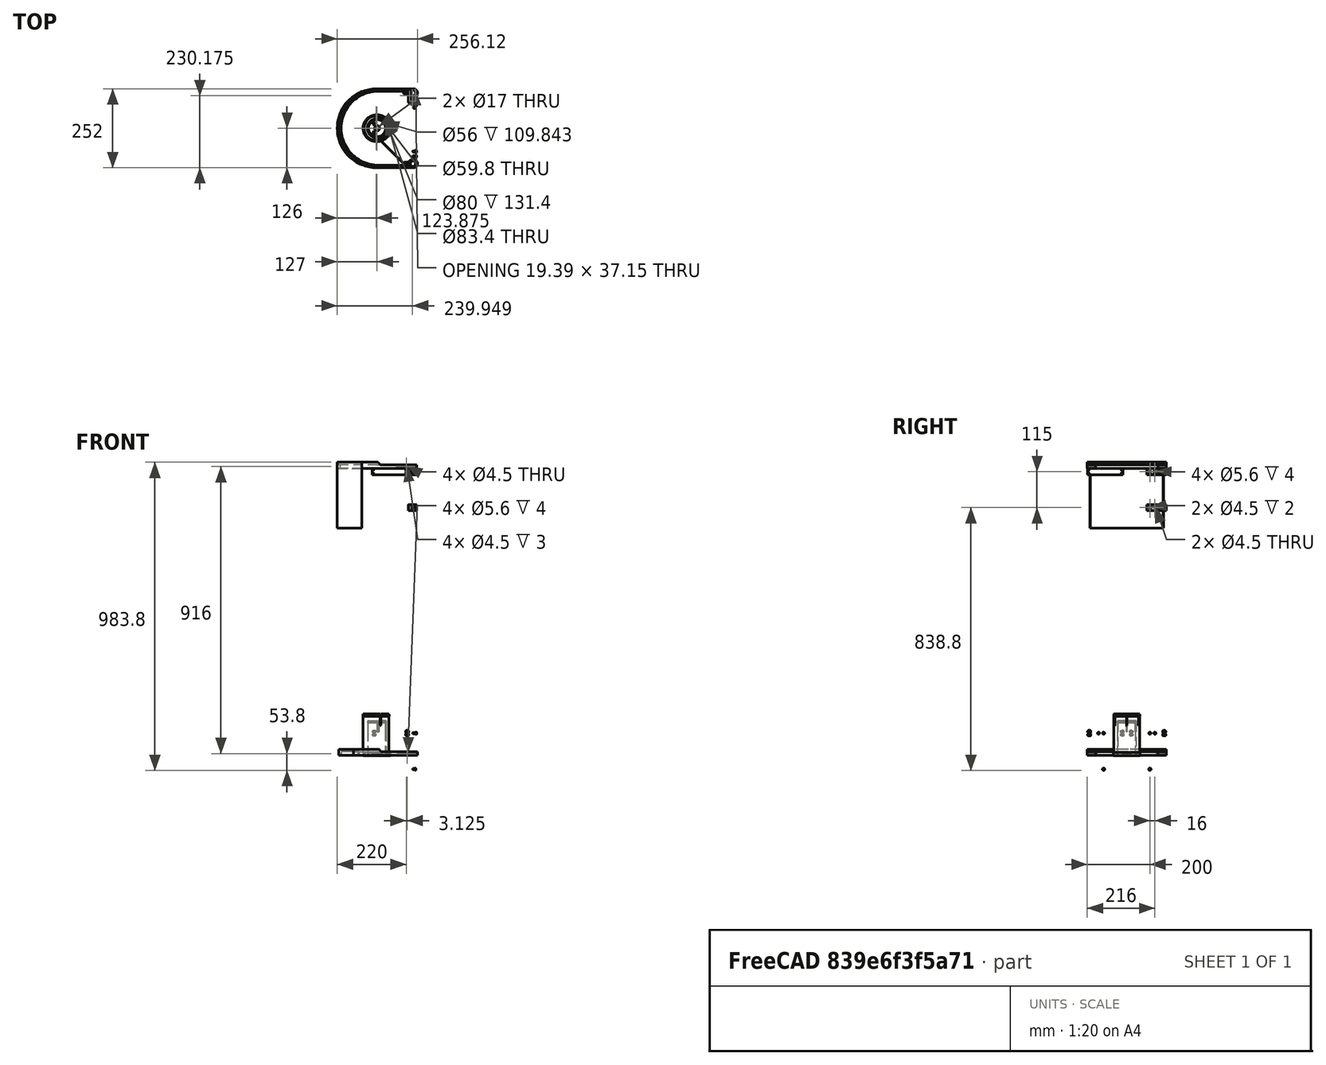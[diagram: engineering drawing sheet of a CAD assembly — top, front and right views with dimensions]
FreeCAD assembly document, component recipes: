
FREECAD ASSEMBLY — COMPONENT RECIPES ("Secondary")

This assembly document has 9 components, labeled P0..P8 below (a component is one placed body or linked part). 9 of them carry a construction recipe — the FreeCAD feature program that regenerates the part from scratch, quoted from this document or its linked companion documents; the rest are supplied as boundary geometry only. No exploded tour is included for this assembly.
COMPONENT P0 — recipe-attached ("SpiderVane", modeled in this document).
Construction recipe (the document's own serialized feature program — sketch geometry with constraints, then the solid features built on it; lengths are millimeters unless a unit is written):

FEATURE [PartDesign::ShapeBinder] ShapeBinder001  label="SpiderVane_ShapeBinder_Spider"
  Support = -> [Binder]
  TraceSupport = false
FEATURE [Sketcher::SketchObject] Sketch075  label="SpiderVane_Base_Sketch"
  ExternalGeometry = -> [ShapeBinder001]
  FullyConstrained = true
  MapMode = 5
  Support = -> [XY_Plane013]
  expr: Constraints[13] = <<Common>>#<<Parameters>>.sec_spiderwidth * 1.5
  expr: Constraints[5] = <<Common>>#<<Parameters>>.sec_spiderwidth
  expr: Constraints[6] = <<Common>>#<<Parameters>>.sec_sidebolt * 2.5
  sketch-geometry (5):
    g0: LineSegment StartX=-11.9668 StartY=-13.1925 StartZ=0 EndX=100.487 EndY=-125.646 EndZ=0
    g1: LineSegment StartX=100.487 StartY=-125.646 StartZ=0 EndX=101.194 EndY=-124.939 EndZ=0
    g2: LineSegment StartX=-11.9668 StartY=-13.1925 StartZ=0 EndX=-11.2596 EndY=-12.4854 EndZ=0
    g3: GeomPoint X=-4.18858 Y=-19.5565 Z=0
    g4: LineSegment StartX=-11.2596 StartY=-12.4854 StartZ=0 EndX=101.194 EndY=-124.939 EndZ=0
  constraints (15):
    c: Coincident(g2,g0)
    c: Perpendicular(g0,g2)
    c: Coincident(g0,g1)
    c: Coincident(g4,g2)
    c: Coincident(g4,g1)
    c: Distance(g1) = 1
    c: Distance(g2,g3) = 10
    c: Perpendicular(g4,g1)
    c: Parallel(g0,g4)
    c: PointOnObject(g3,g-3)
    c: PointOnObject(g3,g-5)
    c: PointOnObject(g2,g-3)
    c: PointOnObject(g1,g-3)
    c: Distance(g1,g-4) = 1.5
    c: Block(g1)
FEATURE [PartDesign::Pad] Pad011  label="SpiderVane_Base"
  Direction = (0,0,1)
  Length = 20
  Length2 = 100
  Profile = -> Sketch075
  Type = 0
  expr: Length = <<Common>>#<<Parameters>>.sec_stalkheight
FEATURE [Sketcher::SketchObject] Sketch076  label="SpiderVane_Hole_Sketch"
  ExternalGeometry = -> [Pad011]
  FullyConstrained = true
  MapMode = 5
  Placement = pos=(-12.5796,-12.5796,0) rot=(0.862856,-0.357407,-0.357407;1.71777rad)
  Support = -> [Pad011]
  expr: Constraints[0] = <<Common>>#<<Parameters>>.sec_collbolt * 1.1
  expr: Constraints[10] = <<Common>>#<<Parameters>>.sec_stalkheight / 2
  expr: Constraints[11] = <<Common>>#<<Parameters>>.sec_stalkheight / 2
  expr: Constraints[14] = <<Common>>#<<Parameters>>.sec_stalkheight / 4
  expr: Constraints[15] = <<Common>>#<<Parameters>>.sec_stalkheight / 4
  expr: Constraints[16] = <<Common>>#<<Parameters>>.sec_sidebolt * 1.25
  expr: Constraints[17] = <<Common>>#<<Parameters>>.sec_sidebolt * 1.25
  sketch-geometry (6):
    g0: Circle CenterX=5.86674 CenterY=15 CenterZ=0 NormalX=0 NormalY=0 NormalZ=1 AngleXU=0 Radius=2.2
    g1: Circle CenterX=5.86674 CenterY=5 CenterZ=0 NormalX=0 NormalY=0 NormalZ=1 AngleXU=0 Radius=2.2
    g2: Circle CenterX=154.901 CenterY=15 CenterZ=0 NormalX=0 NormalY=0 NormalZ=1 AngleXU=0 Radius=2.2
    g3: Circle CenterX=154.901 CenterY=5 CenterZ=0 NormalX=0 NormalY=0 NormalZ=1 AngleXU=0 Radius=2.2
    g4: LineSegment StartX=5.86674 StartY=15 StartZ=0 EndX=5.86674 EndY=0 EndZ=0
    g5: LineSegment StartX=154.901 StartY=15 StartZ=0 EndX=154.901 EndY=0 EndZ=0
  constraints (18):
    c: Diameter(g2) = 4.4
    c: Equal(g2,g3)
    c: Equal(g2,g0)
    c: Equal(g2,g1)
    c: Coincident(g4,g0)
    c: PointOnObject(g4,g-1)
    c: Vertical(g4)
    c: Coincident(g5,g2)
    c: PointOnObject(g5,g-1)
    c: Vertical(g5)
    c: DistanceY(g1,g0) = 10
    c: DistanceY(g3,g2) = 10
    c: PointOnObject(g1,g4)
    c: PointOnObject(g3,g5)
    c: DistanceY(g4,g1) = 5
    c: DistanceY(g5,g3) = 5
    c: DistanceX(g-3,g4) = 5
    c: DistanceX(g5,g-4) = 5
FEATURE [PartDesign::Hole] Hole032  label="SpiderVane_Hole"
  BaseFeature = -> Pad011
  CustomThreadClearance = 0
  Depth = 25
  DepthType = 1
  Diameter = 4.3
  DrillForDepth = false
  DrillPoint = 1
  DrillPointAngle = 118
  HoleCutCountersinkAngle = 90
  HoleCutCustomValues = false
  HoleCutDepth = 0
  HoleCutDiameter = 6.1
  HoleCutType = 0
  ModelThread = false
  Profile = -> Sketch076
  Tapered = false
  TaperedAngle = 90
  ThreadClass = 0
  ThreadDepth = 23.5
  ThreadDepthType = 0
  ThreadDirection = 0
  ThreadFit = 1
  ThreadSize = 11
  ThreadType = 1
  Threaded = false
  UseCustomThreadClearance = false
FEATURE [PartDesign::CoordinateSystem] Local_CS146  label="LCS_Vane_HubZF"
  AttacherType = Attacher::AttachEngine3D
  MapMode = 11
  Placement = pos=(-8.43122,-16.728,15) rot=(0.281085,0.678598,-0.678598;3.68962rad)
  Support = -> [Hole032]
FEATURE [PartDesign::CoordinateSystem] Local_CS147  label="LCS_Vane_HubZA"
  AttacherType = Attacher::AttachEngine3D
  MapMode = 11
  Placement = pos=(-7.72411,-16.0209,15) rot=(-0.862856,0.357407,-0.357407;1.71777rad)
  Support = -> [Hole032]
FEATURE [PartDesign::CoordinateSystem] Local_CS148  label="LCS_Vane_HubNF"
  AttacherType = Attacher::AttachEngine3D
  MapMode = 11
  Placement = pos=(-8.43122,-16.728,5) rot=(0.281085,0.678598,-0.678598;3.68962rad)
  Support = -> [Hole032]
FEATURE [PartDesign::CoordinateSystem] Local_CS149  label="LCS_Vane_HubNA"
  AttacherType = Attacher::AttachEngine3D
  MapMode = 11
  Placement = pos=(-7.72411,-16.0209,5) rot=(-0.862856,0.357407,-0.357407;1.71777rad)
  Support = -> [Hole032]
FEATURE [PartDesign::CoordinateSystem] Local_CS150  label="LCS_Vane_ClampZF"
  AttacherType = Attacher::AttachEngine3D
  MapMode = 11
  Placement = pos=(96.9516,-122.111,15) rot=(0.281085,0.678598,-0.678598;3.68962rad)
  Support = -> [Hole032]
FEATURE [PartDesign::CoordinateSystem] Local_CS151  label="LCS_Vane_ClampZA"
  AttacherType = Attacher::AttachEngine3D
  MapMode = 11
  Placement = pos=(97.6587,-121.404,15) rot=(-0.862856,0.357407,-0.357407;1.71777rad)
  Support = -> [Hole032]
FEATURE [PartDesign::CoordinateSystem] Local_CS152  label="LCS_Vane_ClampNF"
  AttacherType = Attacher::AttachEngine3D
  MapMode = 11
  Placement = pos=(96.9516,-122.111,5) rot=(0.281085,0.678598,-0.678598;3.68962rad)
  Support = -> [Hole032]
FEATURE [PartDesign::CoordinateSystem] Local_CS153  label="LCS_Vane_ClampNA"
  AttacherType = Attacher::AttachEngine3D
  MapMode = 11
  Placement = pos=(97.6587,-121.404,5) rot=(-0.862856,0.357407,-0.357407;1.71777rad)
  Support = -> [Hole032]
FEATURE [PartDesign::Body] Body011  label="SpiderVane"
  Group = -> [Sketch075,Pad011,Sketch076,Local_CS146,Local_CS147,Local_CS148,Local_CS149,Local_CS150,Local_CS151,Local_CS152,Local_CS153,Hole032,ShapeBinder001]
  Origin = -> Origin013
  Placement = pos=(-3.125,0,896) rot=(0,0,1;0rad)
  Tip = -> Hole032
  expr: .Placement.Base.x = -<<Common>>#<<Parameters>>.sec_offset_x
  expr: .Placement.Base.z = <<Common>>#<<Parameters>>.datum_sec_upperhub
COMPONENT P1 — recipe-attached ("UpperClamp", modeled in this document).
Construction recipe (the document's own serialized feature program — sketch geometry with constraints, then the solid features built on it; lengths are millimeters unless a unit is written):

FEATURE [PartDesign::ShapeBinder] ShapeBinder002  label="UpperClamp_ShapeBinder_Spider"
  Support = -> [Binder]
  TraceSupport = false
FEATURE [Sketcher::SketchObject] Sketch086  label="UpperClamp_Structure_Sketch"
  ExternalGeometry = -> [ShapeBinder002]
  FullyConstrained = true
  MapMode = 5
  Support = -> [XY_Plane060]
  expr: Constraints[18] = <<Common>>#<<Parameters>>.sec_fthick - <<Common>>#<<Parameters>>.pri_tol
  expr: Constraints[19] = <<Common>>#<<Parameters>>.sec_spthick
  expr: Constraints[31] = <<Common>>#<<Parameters>>.sec_fthick + 4 - <<Common>>#<<Parameters>>.sec_sidebolt * 1.25
  expr: Constraints[38] = <<Common>>#<<Parameters>>.sec_fillet
  expr: Constraints[39] = <<Common>>#<<Parameters>>.sec_sidebolt * 5.5
  expr: Constraints[40] = <<Common>>#<<Parameters>>.sec_fillet
  expr: Constraints[47] = <<Common>>#<<Parameters>>.sec_fthick / 2
  expr: Constraints[58] = <<Common>>#<<Parameters>>.sec_fillet / 2
  expr: Constraints[59] = <<Common>>#<<Parameters>>.sec_fthick * 1.5
  expr: Constraints[60] = <<Common>>#<<Parameters>>.sec_fthick * 2
  expr: Constraints[68] = <<Common>>#<<Parameters>>.sec_sidebolt_y
  expr: Constraints[6] = <<Common>>#<<Parameters>>.sec_sidebolt * 2.5 + <<Common>>#<<Parameters>>.sec_spiderwidth * 1.5
  expr: Constraints[70] = <<Common>>#<<Parameters>>.sec_fthick * 2
  expr: Constraints[88] = <<Common>>#<<Parameters>>.sec_sidebolt * 3.5 - <<Common>>#<<Parameters>>.sec_fillet
  expr: Constraints[93] = <<Common>>#<<Parameters>>.sec_sidebolt_y - <<Common>>#<<Parameters>>.sec_sidebolt * 6
  sketch-geometry (34):
    g0: LineSegment StartX=124.125 StartY=100.5 StartZ=0 EndX=124.125 EndY=64 EndZ=0
    g1: LineSegment StartX=118.125 StartY=103.094 StartZ=0 EndX=118.125 EndY=86 EndZ=0
    g2: ArcOfCircle CenterX=116.125 CenterY=113 CenterZ=0 NormalX=0 NormalY=0 NormalZ=1 AngleXU=0 Radius=13 StartAngle=0 EndAngle=1.5708
    g3: LineSegment StartX=116.125 StartY=126 StartZ=0 EndX=102.255 EndY=126 EndZ=0
    g4: LineSegment StartX=94.1232 StartY=117.868 StartZ=0 EndX=106.508 EndY=104.253 EndZ=0
    g5: LineSegment StartX=102.255 StartY=126 StartZ=0 EndX=94.1232 EndY=117.868 EndZ=0
    g6: LineSegment StartX=120.125 StartY=64 StartZ=0 EndX=124.125 EndY=64 EndZ=0
    g7: LineSegment StartX=116.125 StartY=126 StartZ=0 EndX=116.125 EndY=113 EndZ=0
    g8: LineSegment StartX=116.125 StartY=113 StartZ=0 EndX=129.125 EndY=113 EndZ=0
    g9: LineSegment StartX=124.125 StartY=100.5 StartZ=0 EndX=125.125 EndY=100.5 EndZ=0
    g10: LineSegment StartX=129.125 StartY=113 StartZ=0 EndX=129.125 EndY=109.881 EndZ=0
    g11: ArcOfCircle CenterX=116.125 CenterY=109.881 CenterZ=0 NormalX=0 NormalY=0 NormalZ=1 AngleXU=0 Radius=13 StartAngle=5.47707 EndAngle=6.28319
    g12: LineSegment StartX=116.125 StartY=109.881 StartZ=0 EndX=129.125 EndY=109.881 EndZ=0
    g13: LineSegment StartX=102.255 StartY=126 StartZ=0 EndX=92.709 EndY=116.454 EndZ=0
    g14: LineSegment StartX=92.709 StartY=116.454 StartZ=0 EndX=111.539 EndY=97.6238 EndZ=0
    g15: LineSegment StartX=112.125 StartY=96.2096 StartZ=0 EndX=112.125 EndY=83.6569 EndZ=0
    g16: LineSegment StartX=116.625 StartY=102.662 StartZ=0 EndX=116.625 EndY=86 EndZ=0
    g17: ArcOfCircle CenterX=120.125 CenterY=66 CenterZ=0 NormalX=0 NormalY=0 NormalZ=1 AngleXU=0 Radius=2 StartAngle=3.14159 EndAngle=4.71239
    g18: ArcOfCircle CenterX=110.125 CenterY=96.2096 CenterZ=0 NormalX=0 NormalY=0 NormalZ=1 AngleXU=0 Radius=2 StartAngle=1.6e-15 EndAngle=0.785398
    g19: ArcOfCircle CenterX=116.125 CenterY=113 CenterZ=0 NormalX=0 NormalY=0 NormalZ=1 AngleXU=0 Radius=9.35 StartAngle=5.00646 EndAngle=10.9472
    g20: LineSegment StartX=118.125 StartY=86 StartZ=0 EndX=116.625 EndY=86 EndZ=0
    g21: LineSegment StartX=118.125 StartY=66 StartZ=0 EndX=120.125 EndY=66 EndZ=0
    g22: LineSegment StartX=120.125 StartY=66 StartZ=0 EndX=120.125 EndY=64 EndZ=0
    g23: ArcOfCircle CenterX=115.625 CenterY=102.662 CenterZ=0 NormalX=0 NormalY=0 NormalZ=1 AngleXU=0 Radius=1 StartAngle=1.2e-15 EndAngle=1.52247
    g24: ArcOfCircle CenterX=119.125 CenterY=103.094 CenterZ=0 NormalX=0 NormalY=0 NormalZ=1 AngleXU=0 Radius=1 StartAngle=1.86487 EndAngle=3.14159
    g25: LineSegment StartX=112.125 StartY=90 StartZ=0 EndX=116.625 EndY=90 EndZ=0
    g26: ArcOfCircle CenterX=114.125 CenterY=83.6569 CenterZ=0 NormalX=0 NormalY=0 NormalZ=1 AngleXU=0 Radius=2 StartAngle=3.14159 EndAngle=3.92699
    g27: ArcOfCircle CenterX=116.125 CenterY=76 CenterZ=0 NormalX=0 NormalY=0 NormalZ=1 AngleXU=0 Radius=2 StartAngle=-1.8e-15 EndAngle=0.785398
    g28: LineSegment StartX=112.711 StartY=82.2426 StartZ=0 EndX=117.539 EndY=77.4142 EndZ=0
    g29: LineSegment StartX=118.125 StartY=76 StartZ=0 EndX=118.125 EndY=66 EndZ=0
    g30: LineSegment StartX=112.125 StartY=83.6569 StartZ=0 EndX=114.125 EndY=83.6569 EndZ=0
    g31: LineSegment StartX=114.125 StartY=83.6569 StartZ=0 EndX=112.711 EndY=82.2426 EndZ=0
    g32: LineSegment StartX=117.539 StartY=77.4142 StartZ=0 EndX=116.125 EndY=76 EndZ=0
    g33: LineSegment StartX=116.125 StartY=76 StartZ=0 EndX=118.125 EndY=76 EndZ=0
  constraints (96):
    c: Vertical(g0)
    c: Vertical(g1)
    c: Coincident(g3,g2)
    c: Horizontal(g3)
    c: Coincident(g5,g3)
    c: Coincident(g5,g4)
    c: Distance(g5) = 11.5
    c: Horizontal(g6)
    c: Vertical(g7)
    c: Coincident(g7,g2)
    c: PointOnObject(g4,g-6)
    c: Parallel(g5,g-6)
    c: Coincident(g2,g-4)
    c: PointOnObject(g0,g-5)
    c: Coincident(g8,g2)
    c: Horizontal(g8)
    c: Coincident(g9,g0)
    c: Horizontal(g9)
    c: DistanceY(g0,g-5) = 2.5
    c: DistanceX(g9,g9) = 1
    c: Coincident(g10,g2)
    c: Vertical(g10)
    c: Coincident(g11,g10)
    c: Coincident(g11,g9)
    c: Coincident(g12,g11)
    c: Coincident(g12,g10)
    c: Horizontal(g12)
    c: Equal(g11,g2)
    c: PointOnObject(g2,g-4)
    c: Coincident(g13,g3)
    c: PointOnObject(g13,g-6)
    c: Distance(g13,g4) = 2
    c: Coincident(g14,g13)
    c: Tangent(g4,g-4)
    c: PointOnObject(g4,g-4)
    c: Perpendicular(g-6,g14)
    c: Vertical(g15)
    c: Vertical(g16)
    c: Radius(g17) = 2
    c: DistanceY(g6,g16) = 22
    c: Radius(g18) = 2
    c: Tangent(g18,g15) = 1.5708
    c: Tangent(g18,g14) = 1.5708
    c: Coincident(g19,g2)
    c: Coincident(g20,g1)
    c: Coincident(g20,g16)
    c: Horizontal(g20)
    c: DistanceX(g20,g20) = 1.5
    c: Coincident(g17,g6)
    c: Coincident(g21,g17)
    c: Horizontal(g21)
    c: Coincident(g22,g17)
    c: Coincident(g22,g6)
    c: Vertical(g22)
    c: Coincident(g7,g2)
    c: Coincident(g7,g8)
    c: Tangent(g19,g23) = 1.5708
    c: Tangent(g16,g23) = 1.5708
    c: Radius(g23) = 1
    c: DistanceX(g15,g16) = 4.5
    c: DistanceX(g1,g0) = 6
    c: Tangent(g19,g24) = 1.5708
    c: Tangent(g1,g24) = -1.5708
    c: Equal(g24,g23)
    c: PointOnObject(g19,g-3)
    c: PointOnObject(g25,g15)
    c: Horizontal(g25)
    c: PointOnObject(g25,g16)
    c: DistanceY(g25) = 90
    c: Coincident(g17,g21)
    c: DistanceX(g17,g0) = 6
    c: Coincident(g26,g15)
    c: Coincident(g28,g26)
    c: Coincident(g28,g27)
    c: Coincident(g29,g27)
    c: Coincident(g29,g17)
    c: Vertical(g29)
    c: Coincident(g30,g15)
    c: Coincident(g30,g26)
    c: Coincident(g31,g26)
    c: Coincident(g31,g26)
    c: Coincident(g32,g27)
    c: Coincident(g32,g27)
    c: Coincident(g33,g27)
    c: Coincident(g33,g27)
    c: Horizontal(g33)
    c: Horizontal(g30)
    c: Equal(g26,g27)
    c: DistanceY(g6,g27) = 12
    c: Perpendicular(g28,g32)
    c: Perpendicular(g28,g31)
    c: Angle(g30,g31) = 0.785398
    c: DistanceX(g15,g17) = 6  'ClampHeight'
    c: DistanceY(g17) = 66
    c: Coincident(g6,g0)
    c: Equal(g27,g17)
FEATURE [PartDesign::Plane] DatumPlane025  label="UpperClamp_DatumPlane_Side"
  AttachmentOffset = pos=(0,0,0) rot=(0,0,1;1.5708rad)
  Length = 67.3781
  MapMode = 14
  Placement = pos=(124.125,0,0) rot=(0.707107,0,0.707107;3.14159rad)
  ResizeMode = 0
  Support = -> [ShapeBinder002,X_Axis060]
  Width = 168.378
FEATURE [Sketcher::SketchObject] Sketch085  label="UpperClamp_SideHole_Sketch"
  FullyConstrained = true
  MapMode = 5
  Placement = pos=(124.125,0,0) rot=(0.707107,0,0.707107;3.14159rad)
  Support = -> [DatumPlane025]
  expr: Constraints[0] = <<Common>>#<<Parameters>>.sec_sidebolt * 1.1
  expr: Constraints[5] = <<Common>>#<<Parameters>>.sec_stalkheight / 2
  expr: Constraints[6] = <<Common>>#<<Parameters>>.sec_sidebolt * 4
  expr: Constraints[7] = <<Common>>#<<Parameters>>.sec_sidebolt_y
  sketch-geometry (3):
    g0: Circle CenterX=10 CenterY=-74 CenterZ=0 NormalX=0 NormalY=0 NormalZ=1 AngleXU=0 Radius=2.2
    g1: Circle CenterX=10 CenterY=-90 CenterZ=0 NormalX=0 NormalY=0 NormalZ=1 AngleXU=0 Radius=2.2
    g2: LineSegment StartX=10 StartY=-74 StartZ=0 EndX=10 EndY=-90 EndZ=0
  constraints (8):
    c: Diameter(g0) = 4.4
    c: Equal(g0,g1)
    c: Coincident(g2,g0)
    c: Coincident(g2,g1)
    c: Vertical(g2)
    c: DistanceX(g2) = 10
    c: DistanceY(g2,g2) = 16
    c: DistanceY(g1,g-1) = 90
FEATURE [PartDesign::Pad] Pad031  label="UpperClamp_Structure"
  Direction = (0,0,1)
  Length = 20
  Length2 = 100
  Profile = -> Sketch086
  Type = 0
  expr: Length = <<Common>>#<<Parameters>>.sec_stalkheight
FEATURE [PartDesign::Plane] DatumPlane026  label="UpperClamp_DatumPlane_Spider"
  Length = 236.529
  MapMode = 14
  Placement = pos=(-11.8725,11.8725,0) rot=(-0.281085,0.678598,0.678598;3.68962rad)
  ResizeMode = 0
  Support = -> [ShapeBinder002,Z_Axis060]
  Width = 70.7729
FEATURE [Sketcher::SketchObject] Sketch087  label="UpperClamp_SpiderHole_Sketch"
  ExternalGeometry = -> [ShapeBinder002]
  FullyConstrained = true
  MapMode = 5
  Placement = pos=(-11.8725,11.8725,0) rot=(-0.281085,0.678598,0.678598;3.68962rad)
  Support = -> [DatumPlane026]
  expr: Constraints[0] = <<Common>>#<<Parameters>>.sec_collbolt * 1.1
  expr: Constraints[2] = <<Common>>#<<Parameters>>.sec_stalkheight / 2
  expr: Constraints[7] = <<Common>>#<<Parameters>>.sec_stalkheight / 4
  expr: Constraints[8] = <<Common>>#<<Parameters>>.sec_sidebolt * 1.25 + <<Common>>#<<Parameters>>.sec_spiderwidth * 1.5
  sketch-geometry (3):
    g0: Circle CenterX=-154.901 CenterY=5 CenterZ=0 NormalX=0 NormalY=0 NormalZ=1 AngleXU=0 Radius=2.2
    g1: Circle CenterX=-154.901 CenterY=15 CenterZ=0 NormalX=0 NormalY=0 NormalZ=1 AngleXU=0 Radius=2.2
    g2: LineSegment StartX=-154.901 StartY=15 StartZ=0 EndX=-154.901 EndY=0 EndZ=0
  constraints (9):
    c: Diameter(g0) = 4.4
    c: Equal(g0,g1)
    c: DistanceY(g0,g1) = 10
    c: Coincident(g2,g1)
    c: PointOnObject(g2,g-1)
    c: PointOnObject(g0,g2)
    c: Vertical(g2)
    c: DistanceY(g2,g0) = 5
    c: DistanceX(g-3,g2) = 6.5
FEATURE [PartDesign::Plane] DatumPlane032  label="UpperClamp_DatumPlane_SpiderNut"
  AttachmentOffset = pos=(0,0,-3) rot=(0,0,1;0rad)
  Length = 236.529
  MapMode = 5
  Placement = pos=(-9.75121,9.75121,0) rot=(-0.281085,0.678598,0.678598;3.68962rad)
  ResizeMode = 0
  Support = -> [DatumPlane026]
  Width = 70.7729
  expr: .AttachmentOffset.Base.z = -<<Common>>#<<Parameters>>.sec_fthick
FEATURE [PartDesign::CoordinateSystem] Local_CS275  label="LCS_UpperClamp_PoleTop"
  AttacherType = Attacher::AttachEngine3D
  AttachmentOffset = pos=(0,0,20) rot=(0,0,1;0rad)
  MapMode = 11
  Placement = pos=(116.125,113,20) rot=(0,0,1;1.5708rad)
  Support = -> [ShapeBinder002]
  expr: .AttachmentOffset.Base.z = <<Common>>#<<Parameters>>.sec_stalkheight
FEATURE [PartDesign::CoordinateSystem] Local_CS290  label="LCS_UpperClamp_PoleBottom"
  AttacherType = Attacher::AttachEngine3D
  MapMode = 11
  Placement = pos=(116.125,113,0) rot=(0.707107,-0.707107,0;3.14159rad)
  Support = -> [ShapeBinder002]
FEATURE [Sketcher::SketchObject] Sketch284  label="UpperClamp_SpiderNut_Sketch"
  AttachmentOffset = pos=(0,0,-3) rot=(0,0,1;0rad)
  ExternalGeometry = -> [Sketch087]
  FullyConstrained = true
  MapMode = 5
  Placement = pos=(-9.75121,9.75121,0) rot=(-0.281085,0.678598,0.678598;3.68962rad)
  Support = -> [DatumPlane026]
  expr: Constraints[14] = 7 + Common#<<Parameters>>.acc_FDMtol
  expr: Constraints[28] = <<Common>>#<<Parameters>>.sec_stalkheight / 4 + 1
  sketch-geometry (21):
    g0: LineSegment StartX=-158.551 StartY=21 StartZ=0 EndX=-158.551 EndY=11.35 EndZ=0
    g1: LineSegment StartX=-158.551 StartY=11.35 StartZ=0 EndX=-151.251 EndY=11.35 EndZ=0
    g2: LineSegment StartX=-151.251 StartY=11.35 StartZ=0 EndX=-151.251 EndY=21 EndZ=0
    g3: LineSegment StartX=-151.251 StartY=21 StartZ=0 EndX=-158.551 EndY=21 EndZ=0
    g4: LineSegment StartX=-158.551 StartY=-1 StartZ=0 EndX=-158.551 EndY=8.65 EndZ=0
    g5: LineSegment StartX=-158.551 StartY=8.65 StartZ=0 EndX=-151.251 EndY=8.65 EndZ=0
    g6: LineSegment StartX=-151.251 StartY=8.65 StartZ=0 EndX=-151.251 EndY=-1 EndZ=0
    g7: LineSegment StartX=-151.251 StartY=-1 StartZ=0 EndX=-158.551 EndY=-1 EndZ=0
    g8: LineSegment StartX=-154.901 StartY=15 StartZ=0 EndX=-154.901 EndY=5 EndZ=0
    g9: LineSegment StartX=-158.551 StartY=8.65 StartZ=0 EndX=-154.901 EndY=5 EndZ=0
    g10: LineSegment StartX=-154.901 StartY=15 StartZ=0 EndX=-151.251 EndY=11.35 EndZ=0
    g11: LineSegment StartX=-158.551 StartY=21 StartZ=0 EndX=-158.551 EndY=12.8927 EndZ=0
    g12: LineSegment StartX=-151.251 StartY=21 StartZ=0 EndX=-151.251 EndY=12.8927 EndZ=0
    g13: LineSegment StartX=-151.251 StartY=-1 StartZ=0 EndX=-151.251 EndY=7.10733 EndZ=0
    g14: LineSegment StartX=-158.551 StartY=-1 StartZ=0 EndX=-158.551 EndY=7.10733 EndZ=0
    g15: LineSegment StartX=-158.551 StartY=7.10733 StartZ=0 EndX=-154.901 EndY=9.21466 EndZ=0
    g16: LineSegment StartX=-151.251 StartY=7.10733 StartZ=0 EndX=-154.901 EndY=9.21466 EndZ=0
    g17: LineSegment StartX=-158.551 StartY=12.8927 StartZ=0 EndX=-154.901 EndY=10.7853 EndZ=0
    g18: LineSegment StartX=-151.251 StartY=12.8927 StartZ=0 EndX=-154.901 EndY=10.7853 EndZ=0
    g19: LineSegment StartX=-154.901 StartY=15 StartZ=0 EndX=-151.251 EndY=12.8927 EndZ=0
    g20: LineSegment StartX=-151.251 StartY=7.10733 StartZ=0 EndX=-154.901 EndY=5 EndZ=0
  constraints (55):
    c: Vertical(g0)
    c: Coincident(g2,g1)
    c: Vertical(g2)
    c: Coincident(g3,g2)
    c: Coincident(g3,g0)
    c: Vertical(g4)
    c: Coincident(g6,g5)
    c: Vertical(g6)
    c: Coincident(g7,g6)
    c: Coincident(g7,g4)
    c: Horizontal(g3)
    c: Equal(g3,g7)
    c: Horizontal(g7)
    c: Equal(g4,g0)
    c: DistanceX(g3,g3) = 7.3
    c: Coincident(g5,g4)
    c: Coincident(g1,g0)
    c: Horizontal(g5)
    c: Symmetric(g0,g1,g8)
    c: PointOnObject(g4,g0)
    c: Coincident(g8,g-4)
    c: Coincident(g8,g-3)
    c: Coincident(g9,g4)
    c: Coincident(g9,g8)
    c: Coincident(g10,g8)
    c: Coincident(g10,g1)
    c: Equal(g9,g10)
    c: Angle(g8,g10) = 0.785398
    c: DistanceY(g8,g2) = 6
    c: Coincident(g11,g3)
    c: Vertical(g11)
    c: Coincident(g12,g3)
    c: Vertical(g12)
    c: Coincident(g13,g7)
    c: Vertical(g13)
    c: Coincident(g14,g7)
    c: Vertical(g14)
    c: Coincident(g15,g14)
    c: PointOnObject(g15,g8)
    c: Coincident(g16,g13)
    c: Coincident(g16,g15)
    c: Coincident(g17,g11)
    c: PointOnObject(g17,g8)
    c: Coincident(g18,g12)
    c: Coincident(g18,g17)
    c: Equal(g18,g17)
    c: Equal(g17,g15)
    c: Equal(g15,g16)
    c: Angle(g18,g17) = 2.0944
    c: Coincident(g19,g8)
    c: Coincident(g19,g12)
    c: Coincident(g20,g13)
    c: Coincident(g20,g8)
    c: Equal(g20,g16)
    c: Equal(g18,g19)
FEATURE [Sketcher::SketchObject] Sketch  label="UpperClamp_ClampBump_Sketch"
  AttachmentOffset = pos=(0,0,10) rot=(0,0,1;0rad)
  ExternalGeometry = -> [ShapeBinder002]
  FullyConstrained = true
  MapMode = 5
  Placement = pos=(0,0,10) rot=(0,0,1;0rad)
  Support = -> [XY_Plane060]
  expr: .AttachmentOffset.Base.z = <<Common>>#<<Parameters>>.sec_stalkheight / 2
  expr: Constraints[70] = <<Common>>#<<Parameters>>.sec_poledia
  sketch-geometry (26):
    g0: LineSegment StartX=107.487 StartY=116.578 StartZ=0 EndX=124.763 EndY=109.422 EndZ=0
    g1: LineSegment StartX=112.547 StartY=121.638 StartZ=0 EndX=119.703 EndY=104.362 EndZ=0
    g2: LineSegment StartX=119.703 StartY=121.638 StartZ=0 EndX=112.547 EndY=104.362 EndZ=0
    g3: LineSegment StartX=124.763 StartY=116.578 StartZ=0 EndX=107.487 EndY=109.422 EndZ=0
    g4: LineSegment StartX=107.487 StartY=116.578 StartZ=0 EndX=112.547 EndY=121.638 EndZ=0
    g5: LineSegment StartX=112.547 StartY=121.638 StartZ=0 EndX=119.703 EndY=121.638 EndZ=0
    g6: LineSegment StartX=119.703 StartY=121.638 StartZ=0 EndX=124.763 EndY=116.578 EndZ=0
    g7: LineSegment StartX=124.763 StartY=116.578 StartZ=0 EndX=124.763 EndY=109.422 EndZ=0
    g8: ArcOfCircle CenterX=119.703 CenterY=104.362 CenterZ=0 NormalX=0 NormalY=0 NormalZ=1 AngleXU=0 Radius=0.35 StartAngle=0.411417 EndAngle=3.51557
    g9: ArcOfCircle CenterX=124.763 CenterY=109.422 CenterZ=0 NormalX=0 NormalY=0 NormalZ=1 AngleXU=0 Radius=0.35 StartAngle=1.19681 EndAngle=4.30097
    g10: ArcOfCircle CenterX=124.763 CenterY=116.578 CenterZ=0 NormalX=0 NormalY=0 NormalZ=1 AngleXU=0 Radius=0.35 StartAngle=1.98221 EndAngle=5.08637
    g11: ArcOfCircle CenterX=119.703 CenterY=121.638 CenterZ=0 NormalX=0 NormalY=0 NormalZ=1 AngleXU=0 Radius=0.35 StartAngle=2.76761 EndAngle=5.87177
    g12: ArcOfCircle CenterX=112.547 CenterY=121.638 CenterZ=0 NormalX=0 NormalY=0 NormalZ=1 AngleXU=0 Radius=0.35 StartAngle=3.55301 EndAngle=6.65717
    g13: ArcOfCircle CenterX=107.487 CenterY=116.578 CenterZ=0 NormalX=0 NormalY=0 NormalZ=1 AngleXU=0 Radius=0.35 StartAngle=4.33841 EndAngle=7.44256
    g14: ArcOfCircle CenterX=107.487 CenterY=109.422 CenterZ=0 NormalX=0 NormalY=0 NormalZ=1 AngleXU=0 Radius=0.35 StartAngle=5.12381 EndAngle=8.22796
    g15: ArcOfCircle CenterX=112.547 CenterY=104.362 CenterZ=0 NormalX=0 NormalY=0 NormalZ=1 AngleXU=0 Radius=0.35 StartAngle=5.9092 EndAngle=9.01336
    g16: ArcOfCircle CenterX=116.125 CenterY=113 CenterZ=0 NormalX=0 NormalY=0 NormalZ=1 AngleXU=0 Radius=9.35 StartAngle=5.06765 EndAngle=5.14252
    g17: ArcOfCircle CenterX=116.125 CenterY=113 CenterZ=0 NormalX=0 NormalY=0 NormalZ=1 AngleXU=0 Radius=9.35 StartAngle=5.85305 EndAngle=5.92792
    g18: ArcOfCircle CenterX=116.125 CenterY=113 CenterZ=0 NormalX=0 NormalY=0 NormalZ=1 AngleXU=0 Radius=9.35 StartAngle=0.355264 EndAngle=0.430134
    g19: ArcOfCircle CenterX=116.125 CenterY=113 CenterZ=0 NormalX=0 NormalY=0 NormalZ=1 AngleXU=0 Radius=9.35 StartAngle=1.14066 EndAngle=1.21553
    g20: ArcOfCircle CenterX=116.125 CenterY=113 CenterZ=0 NormalX=0 NormalY=0 NormalZ=1 AngleXU=0 Radius=9.35 StartAngle=1.92606 EndAngle=2.00093
    g21: ArcOfCircle CenterX=116.125 CenterY=113 CenterZ=0 NormalX=0 NormalY=0 NormalZ=1 AngleXU=0 Radius=9.35 StartAngle=2.71146 EndAngle=2.78633
    g22: ArcOfCircle CenterX=116.125 CenterY=113 CenterZ=0 NormalX=0 NormalY=0 NormalZ=1 AngleXU=0 Radius=9.35 StartAngle=3.49686 EndAngle=3.57173
    g23: ArcOfCircle CenterX=116.125 CenterY=113 CenterZ=0 NormalX=0 NormalY=0 NormalZ=1 AngleXU=0 Radius=9.35 StartAngle=4.28225 EndAngle=4.35713
    g24: GeomPoint X=119.569 Y=104.685 Z=0
    g25: GeomPoint X=112.681 Y=121.315 Z=0
  constraints (76):
    c: PointOnObject(g0,g-3)
    c: PointOnObject(g0,g-3)
    c: PointOnObject(g1,g-3)
    c: PointOnObject(g1,g-3)
    c: PointOnObject(g2,g-3)
    c: PointOnObject(g2,g-3)
    c: PointOnObject(g3,g-3)
    c: PointOnObject(g3,g-3)
    c: Coincident(g4,g0)
    c: Coincident(g5,g1)
    c: Coincident(g6,g2)
    c: Coincident(g7,g3)
    c: Coincident(g4,g1)
    c: Coincident(g5,g2)
    c: Coincident(g6,g3)
    c: Equal(g4,g5)
    c: Equal(g5,g6)
    c: Coincident(g7,g0)
    c: Equal(g7,g5)
    c: Horizontal(g5)
    c: Coincident(g8,g1)
    c: PointOnObject(g8,g-3)
    c: Coincident(g9,g0)
    c: PointOnObject(g9,g-3)
    c: Coincident(g10,g3)
    c: PointOnObject(g10,g-3)
    c: Coincident(g11,g2)
    c: PointOnObject(g11,g-3)
    c: Coincident(g12,g1)
    c: PointOnObject(g12,g-3)
    c: Coincident(g13,g0)
    c: PointOnObject(g13,g-3)
    c: Coincident(g14,g3)
    c: PointOnObject(g14,g-3)
    c: Coincident(g15,g2)
    c: PointOnObject(g15,g-3)
    c: Coincident(g16,g8)
    c: Coincident(g16,g8)
    c: Coincident(g17,g16)
    c: Coincident(g17,g9)
    c: Coincident(g17,g9)
    c: Coincident(g18,g16)
    c: Coincident(g18,g10)
    c: Coincident(g18,g10)
    c: Coincident(g19,g16)
    c: Coincident(g19,g11)
    c: Coincident(g19,g11)
    c: Coincident(g20,g16)
    c: Coincident(g20,g12)
    c: Coincident(g20,g12)
    c: Coincident(g21,g16)
    c: Coincident(g21,g13)
    c: Coincident(g21,g13)
    c: Coincident(g22,g16)
    c: Coincident(g22,g14)
    c: Coincident(g22,g14)
    c: Coincident(g23,g16)
    c: Coincident(g23,g15)
    c: Coincident(g23,g15)
    c: Equal(g8,g9)
    c: Equal(g9,g10)
    c: Equal(g10,g11)
    c: Equal(g11,g12)
    c: Equal(g12,g13)
    c: Equal(g13,g14)
    c: Equal(g14,g15)
    c: PointOnObject(g24,g8)
    c: PointOnObject(g24,g1)
    c: PointOnObject(g25,g12)
    c: PointOnObject(g25,g1)
    c: Distance(g25,g24) = 18
    c: PointOnObject(g16,g0)
    c: PointOnObject(g16,g1)
    c: PointOnObject(g16,g2)
    c: PointOnObject(g16,g3)
    c: Coincident(g16,g-3)
FEATURE [PartDesign::Pad] Pad  label="UpperClamp_ClampBump"
  BaseFeature = -> Pad031
  Direction = (0,0,1)
  Length = 18.4
  Length2 = 10
  Midplane = true
  Profile = -> Sketch
  ReferenceAxis = -> Sketch [N_Axis]
  Type = 0
  expr: Length = <<Common>>#<<Parameters>>.sec_stalkheight - 1.6
FEATURE [Sketcher::SketchObject] Sketch285  label="UpperClamp_BumpGrad_Sketch"
  AttachmentOffset = pos=(0,0,0) rot=(1,0,0;1.5708rad)
  ExternalGeometry = -> [ShapeBinder002]
  FullyConstrained = true
  MapMode = 11
  Placement = pos=(116.125,113,0) rot=(0.57735,0.57735,0.57735;2.0944rad)
  Support = -> [ShapeBinder002]
  expr: Constraints[21] = <<Common>>#<<Parameters>>.sec_stalkheight
  expr: Constraints[25] = <<Common>>#<<Parameters>>.sec_poledia / 2
  expr: Constraints[26] = <<Common>>#<<Parameters>>.sec_clamptol * 5
  sketch-geometry (10):
    g0: LineSegment StartX=0 StartY=0 StartZ=0 EndX=0 EndY=20 EndZ=0
    g1: LineSegment StartX=0 StartY=20 StartZ=0 EndX=9.75 EndY=20 EndZ=0
    g2: LineSegment StartX=0 StartY=0 StartZ=0 EndX=9.75 EndY=0 EndZ=0
    g3: LineSegment StartX=9.75 StartY=20 StartZ=0 EndX=9.35 EndY=19.6 EndZ=0
    g4: LineSegment StartX=9.35 StartY=19.6 StartZ=0 EndX=9.35 EndY=19.2 EndZ=0
    g5: LineSegment StartX=9.35 StartY=19.2 StartZ=0 EndX=9 EndY=15.7 EndZ=0
    g6: LineSegment StartX=9 StartY=15.7 StartZ=0 EndX=9 EndY=4.3 EndZ=0
    g7: LineSegment StartX=9 StartY=4.3 StartZ=0 EndX=9.35 EndY=0.8 EndZ=0
    g8: LineSegment StartX=9.35 StartY=0.8 StartZ=0 EndX=9.35 EndY=0.4 EndZ=0
    g9: LineSegment StartX=9.35 StartY=0.4 StartZ=0 EndX=9.75 EndY=0 EndZ=0
  constraints (29):
    c: Coincident(g0,g-1)
    c: Vertical(g0)
    c: Coincident(g1,g0)
    c: Horizontal(g1)
    c: Coincident(g2,g0)
    c: Horizontal(g2)
    c: Coincident(g3,g1)
    c: Coincident(g4,g3)
    c: Vertical(g4)
    c: Coincident(g5,g4)
    c: Coincident(g6,g5)
    c: Vertical(g6)
    c: Coincident(g7,g6)
    c: Coincident(g8,g7)
    c: Vertical(g8)
    c: Coincident(g9,g8)
    c: Coincident(g9,g2)
    c: Equal(g9,g3)
    c: Equal(g8,g4)
    c: Equal(g5,g7)
    c: Equal(g2,g1)
    c: DistanceY(g0,g0) = 20
    c: DistanceY(g4,g4) = 0.4
    c: PointOnObject(g-3,g4)
    c: PointOnObject(g-3,g8)
    c: DistanceX(g5) = 9
    c: DistanceY(g5,g4) = 3.5
    c: Angle(g1,g3) = 0.785398
    c: DistanceY(g3,g1) = 0.4
FEATURE [PartDesign::Line] DatumLine  label="UpperClamp_DatumLine_Pole"
  AttacherType = Attacher::AttachEngineLine
  Length = 20
  MapMode = 19
  Placement = pos=(116.125,113,0) rot=(0,0,1;0rad)
  ResizeMode = 0
  Support = -> [ShapeBinder002]
FEATURE [PartDesign::Groove] Groove  label="UpperClamp_BumpGrad"
  Angle = 360
  Axis = (0,0,1)
  Base = (116.125,113,0)
  BaseFeature = -> Pad
  Profile = -> Sketch285
  ReferenceAxis = -> DatumLine
FEATURE [PartDesign::Hole] Hole  label="UpperClamp_SideHole"
  BaseFeature = -> Groove
  CustomThreadClearance = 0
  Depth = 150.759
  DepthType = 1
  Diameter = 4.5
  DrillForDepth = false
  DrillPoint = 1
  DrillPointAngle = 118
  HoleCutCountersinkAngle = 90
  HoleCutCustomValues = false
  HoleCutDepth = 4
  HoleCutDiameter = 5.6
  HoleCutType = 1
  ModelThread = false
  Profile = -> Sketch085
  Tapered = false
  TaperedAngle = 90
  ThreadClass = 0
  ThreadDepth = 150.759
  ThreadDepthType = 0
  ThreadDirection = 0
  ThreadFit = 0
  ThreadSize = 11
  ThreadType = 1
  Threaded = false
  UseCustomThreadClearance = false
  expr: HoleCutDiameter = <<Common>>#<<Parameters>>.acc_M4Bore
FEATURE [PartDesign::CoordinateSystem] Local_CS176  label="LCS_UpperClampNut_I"
  AttacherType = Attacher::AttachEngine3D
  MapMode = 11
  Placement = pos=(124.125,90,10) rot=(0.57735,-0.57735,-0.57735;2.0944rad)
  Support = -> [Hole]
FEATURE [PartDesign::CoordinateSystem] Local_CS177  label="LCS_UpperClampNut_O"
  AttacherType = Attacher::AttachEngine3D
  MapMode = 11
  Placement = pos=(124.125,74,10) rot=(0.57735,-0.57735,-0.57735;2.0944rad)
  Support = -> [Hole]
FEATURE [PartDesign::CoordinateSystem] Local_CS178  label="LCS_UpperClampBolt_I"
  AttacherType = Attacher::AttachEngine3D
  AttachmentOffset = pos=(0,0,1) rot=(0,0,1;0rad)
  MapMode = 11
  Placement = pos=(125.125,90,10) rot=(0.57735,0.57735,0.57735;2.0944rad)
  Support = -> [Hole]
  expr: .AttachmentOffset.Base.z = <<Common>>#<<Parameters>>.sec_spthick
FEATURE [PartDesign::CoordinateSystem] Local_CS179  label="LCS_UpperClampBolt_O"
  AttacherType = Attacher::AttachEngine3D
  AttachmentOffset = pos=(0,0,1) rot=(0,0,1;0rad)
  MapMode = 11
  Placement = pos=(125.125,74,10) rot=(0.57735,0.57735,0.57735;2.0944rad)
  Support = -> [Hole]
  expr: .AttachmentOffset.Base.z = <<Common>>#<<Parameters>>.sec_spthick
FEATURE [PartDesign::CoordinateSystem] Local_CS181  label="LCS_UpperClampPlate"
  AttacherType = Attacher::AttachEngine3D
  MapMode = 11
  Placement = pos=(124.125,90,10) rot=(0.57735,0.57735,0.57735;2.0944rad)
  Support = -> [Hole]
FEATURE [PartDesign::Hole] Hole052  label="UpperClamp_SpiderHole"
  BaseFeature = -> Hole
  CustomThreadClearance = 0
  Depth = 8
  DepthType = 0
  Diameter = 4.5
  DrillForDepth = false
  DrillPoint = 1
  DrillPointAngle = 118
  HoleCutCountersinkAngle = 90
  HoleCutCustomValues = false
  HoleCutDepth = 0
  HoleCutDiameter = 6.1
  HoleCutType = 0
  ModelThread = false
  Profile = -> Sketch087
  Tapered = false
  TaperedAngle = 90
  ThreadClass = 0
  ThreadDepth = 8
  ThreadDepthType = 0
  ThreadDirection = 0
  ThreadFit = 0
  ThreadSize = 11
  ThreadType = 1
  Threaded = false
  UseCustomThreadClearance = false
FEATURE [PartDesign::CoordinateSystem] Local_CS175  label="LCS_ClampSpider_Z"
  AttacherType = Attacher::AttachEngine3D
  MapMode = 11
  Placement = pos=(97.6587,121.404,15) rot=(-0.862856,-0.357407,0.357407;1.71777rad)
  Support = -> [Hole052]
FEATURE [PartDesign::Pocket] Pocket  label="UpperClamp_SpiderNut"
  BaseFeature = -> Hole052
  Direction = (0.707107,-0.707107,0)
  Length = 3.5
  Length2 = 5
  Profile = -> Sketch284
  ReferenceAxis = -> Sketch284 [N_Axis]
  Type = 0
FEATURE [PartDesign::Chamfer] Chamfer  label="UpperClamp_Chamfer"
  Angle = 45
  Base = -> Pocket [Edge53,Edge50,Edge51,Edge52,Edge46,Edge44,Edge42,Edge40,Edge38,Edge12,Edge6,Edge4,Edge48,Edge49,Edge47,Edge45,Edge43,Edge41,Edge39,Edge37,Edge60,Edge59,Edge57,Edge13,Edge15,Edge17,Edge19,Edge21,Edge23,Edge25,Edge36,Edge35,Edge33,Edge5,Edge3,Edge11,Edge24,Edge22,Edge14,Edge16,+6 more]
  BaseFeature = -> Pocket
  ChamferType = 0
  FlipDirection = false
  Size = 0.4
  Size2 = 1
  SupportTransform = false
  UseAllEdges = false
FEATURE [PartDesign::Body] Body022007  label="UpperClamp"
  Group = -> [Sketch085,Sketch086,DatumPlane025,Pad031,Sketch087,Local_CS175,Local_CS176,Local_CS177,Local_CS178,Local_CS179,Local_CS181,DatumPlane026,ShapeBinder002,DatumPlane032,Local_CS275,Local_CS290,Sketch284,Sketch,Pad,Sketch285,DatumLine,Groove,Hole,Hole052,Pocket,Chamfer]
  Origin = -> Origin060
  Placement = pos=(-3.125,0,896) rot=(0,0,1;0rad)
  Tip = -> Chamfer
  expr: .Placement.Base.x = -<<Common>>#<<Parameters>>.sec_offset_x
  expr: .Placement.Base.z = <<Common>>#<<Parameters>>.datum_sec_upperhub
COMPONENT P2 — recipe-attached ("LowerClamp", modeled in this document).
Construction recipe (the document's own serialized feature program — sketch geometry with constraints, then the solid features built on it; lengths are millimeters unless a unit is written):

FEATURE [PartDesign::ShapeBinder] ShapeBinder008  label="LowerClamp_ShapeBinder"
  Support = -> [Binder]
  TraceSupport = false
FEATURE [PartDesign::Plane] DatumPlane049  label="LowerClamp_DatumPlane_Inner"
  Length = 168.378
  MapMode = 14
  Placement = pos=(103.125,0,0) rot=(0.57735,-0.57735,-0.57735;2.0944rad)
  ResizeMode = 0
  Support = -> [ShapeBinder008,Z_Axis102]
  Width = 67.3781
FEATURE [PartDesign::Plane] DatumPlane050  label="LowerClamp_DatumPlane_Outer"
  AttachmentOffset = pos=(0,0,0) rot=(0,0,1;1.5708rad)
  Length = 67.3781
  MapMode = 14
  Placement = pos=(129.125,0,0) rot=(0.707107,0,0.707107;3.14159rad)
  ResizeMode = 0
  Support = -> [ShapeBinder008,Z_Axis102]
  Width = 168.378
FEATURE [Sketcher::SketchObject] Sketch213  label="LowerClamp_Base_Sketch"
  ExternalGeometry = -> [ShapeBinder008]
  FullyConstrained = true
  MapMode = 5
  Support = -> [XY_Plane101]
  expr: .Constraints.ClampGap = <<Common>>#<<Parameters>>.sec_fthick
  expr: Constraints[17] = <<Common>>#<<Parameters>>.sec_fillet * 2
  expr: Constraints[22] = <<Common>>#<<Parameters>>.sec_spthick
  expr: Constraints[34] = <<Common>>#<<Parameters>>.sec_fthick - <<Common>>#<<Parameters>>.pri_tol
  expr: Constraints[35] = <<Common>>#<<Parameters>>.sec_sidebolt_y - <<Common>>#<<Parameters>>.sec_sidebolt * 6
  expr: Constraints[36] = <<Common>>#<<Parameters>>.sec_fillet
  expr: Constraints[40] = <<Common>>#<<Parameters>>.sec_sidebolt * 4
  expr: Constraints[48] = <<Common>>#<<Parameters>>.sec_fthick * 2
  expr: Constraints[49] = <<Common>>#<<Parameters>>.sec_fillet / 2
  sketch-geometry (18):
    g0: ArcOfCircle CenterX=116.125 CenterY=113 CenterZ=0 NormalX=0 NormalY=0 NormalZ=1 AngleXU=0 Radius=9.35 StartAngle=5.00646 EndAngle=10.8011
    g1: ArcOfCircle CenterX=116.125 CenterY=113 CenterZ=0 NormalX=0 NormalY=0 NormalZ=1 AngleXU=0 Radius=13 StartAngle=1.5e-15 EndAngle=3.14159
    g2: LineSegment StartX=129.125 StartY=113 StartZ=0 EndX=129.125 EndY=109.881 EndZ=0
    g3: LineSegment StartX=118.125 StartY=103.094 StartZ=0 EndX=118.125 EndY=66 EndZ=0
    g4: LineSegment StartX=115.125 StartY=102.845 StartZ=0 EndX=115.125 EndY=80 EndZ=0
    g5: LineSegment StartX=103.125 StartY=113 StartZ=0 EndX=103.125 EndY=84 EndZ=0
    g6: ArcOfCircle CenterX=116.125 CenterY=109.881 CenterZ=0 NormalX=0 NormalY=0 NormalZ=1 AngleXU=0 Radius=13 StartAngle=5.47707 EndAngle=6.28319
    g7: ArcOfCircle CenterX=107.125 CenterY=84 CenterZ=0 NormalX=0 NormalY=0 NormalZ=1 AngleXU=0 Radius=4 StartAngle=3.14159 EndAngle=4.71239
    g8: LineSegment StartX=107.125 StartY=80 StartZ=0 EndX=115.125 EndY=80 EndZ=0
    g9: LineSegment StartX=120.125 StartY=64 StartZ=0 EndX=124.125 EndY=64 EndZ=0
    g10: LineSegment StartX=107.125 StartY=84 StartZ=0 EndX=103.125 EndY=84 EndZ=0
    g11: LineSegment StartX=107.125 StartY=84 StartZ=0 EndX=107.125 EndY=80 EndZ=0
    g12: ArcOfCircle CenterX=120.125 CenterY=66 CenterZ=0 NormalX=0 NormalY=0 NormalZ=1 AngleXU=0 Radius=2 StartAngle=3.14159 EndAngle=4.71239
    g13: LineSegment StartX=124.125 StartY=64 StartZ=0 EndX=124.125 EndY=100.5 EndZ=0
    g14: LineSegment StartX=124.125 StartY=100.5 StartZ=0 EndX=125.125 EndY=100.5 EndZ=0
    g15: LineSegment StartX=103.125 StartY=113 StartZ=0 EndX=129.125 EndY=113 EndZ=0
    g16: ArcOfCircle CenterX=114.125 CenterY=102.845 CenterZ=0 NormalX=0 NormalY=0 NormalZ=1 AngleXU=0 Radius=1 StartAngle=5.9e-15 EndAngle=1.37634
    g17: ArcOfCircle CenterX=119.125 CenterY=103.094 CenterZ=0 NormalX=0 NormalY=0 NormalZ=1 AngleXU=0 Radius=1 StartAngle=1.86487 EndAngle=3.14159
  constraints (50):
    c: Vertical(g2)
    c: Vertical(g3)
    c: Vertical(g4)
    c: Vertical(g5)
    c: Coincident(g7,g5)
    c: Coincident(g8,g7)
    c: Coincident(g8,g4)
    c: Coincident(g10,g7)
    c: Coincident(g10,g5)
    c: Horizontal(g10)
    c: Coincident(g11,g10)
    c: Coincident(g11,g7)
    c: Vertical(g11)
    c: Horizontal(g9)
    c: Horizontal(g8)
    c: Tangent(g3,g12) = -1.5708
    c: Tangent(g9,g12) = -1.5708
    c: Radius(g7) = 4
    c: Coincident(g13,g9)
    c: Vertical(g13)
    c: Coincident(g14,g13)
    c: Horizontal(g14)
    c: DistanceX(g14,g14) = 1
    c: Coincident(g0,g1)
    c: Coincident(g0,g-4)
    c: Equal(g0,g-3)
    c: Equal(g1,g-4)
    c: Coincident(g15,g1)
    c: Coincident(g15,g1)
    c: PointOnObject(g-4,g15)
    c: Horizontal(g15)
    c: Coincident(g5,g15)
    c: Coincident(g2,g15)
    c: PointOnObject(g-5,g13)
    c: DistanceY(g13,g-5) = 2.5
    c: DistanceY(g3) = 66
    c: Radius(g12) = 2
    c: Coincident(g6,g14)
    c: Equal(g-4,g6)
    c: Tangent(g6,g2) = 1.5708
    c: DistanceY(g9,g4) = 16
    c: DistanceX(g5,g3) = 15  'ClampSpace'
    c: DistanceX(g4,g3) = 3  'ClampGap'
    c: Tangent(g4,g16) = 1.5708
    c: Tangent(g0,g16) = 1.5708
    c: Tangent(g3,g17) = -1.5708
    c: Tangent(g0,g17) = 1.5708
    c: Equal(g17,g16)
    c: DistanceX(g3,g9) = 6
    c: Radius(g16) = 1
FEATURE [PartDesign::Pad] Pad057  label="LowerClamp_Base"
  Direction = (0,0,1)
  Length = 20
  Length2 = 100
  Profile = -> Sketch213
  Type = 0
  expr: Length = <<Common>>#<<Parameters>>.sec_clampheight
FEATURE [Sketcher::SketchObject] Sketch214  label="LowerClamp_SideHoles_Sketch"
  FullyConstrained = true
  MapMode = 5
  Placement = pos=(129.125,0,0) rot=(0.707107,0,0.707107;3.14159rad)
  Support = -> [DatumPlane050]
  expr: Constraints[0] = <<Common>>#<<Parameters>>.sec_sidebolt * 1.1
  expr: Constraints[2] = -<<Common>>#<<Parameters>>.sec_sidebolt_y
  expr: Constraints[3] = <<Common>>#<<Parameters>>.sec_sidebolt * 4
  expr: Constraints[7] = <<Common>>#<<Parameters>>.sec_clampheight / 2
  sketch-geometry (3):
    g0: Circle CenterX=10 CenterY=-90 CenterZ=0 NormalX=0 NormalY=0 NormalZ=1 AngleXU=0 Radius=2.2
    g1: Circle CenterX=10 CenterY=-74 CenterZ=0 NormalX=0 NormalY=0 NormalZ=1 AngleXU=0 Radius=2.2
    g2: LineSegment StartX=10 StartY=-74 StartZ=0 EndX=10 EndY=-90 EndZ=0
  constraints (8):
    c: Diameter(g1) = 4.4
    c: Equal(g1,g0)
    c: DistanceY(g0) = -90
    c: DistanceY(g0,g1) = 16
    c: Coincident(g2,g1)
    c: Coincident(g2,g0)
    c: Vertical(g2)
    c: DistanceX(g2) = 10
FEATURE [Sketcher::SketchObject] Sketch215  label="LowerClamp_PlateNut_Sketch"
  AttachmentOffset = pos=(0,0,-15) rot=(0,0,1;0rad)
  FullyConstrained = true
  MapMode = 5
  Placement = pos=(118.125,0,0) rot=(0.57735,-0.57735,-0.57735;2.0944rad)
  Support = -> [DatumPlane049]
  expr: .AttachmentOffset.Base.z = -Sketch213.Constraints.ClampSpace
  expr: Constraints[0] = -(<<Common>>#<<Parameters>>.sec_sidebolt_y - <<Common>>#<<Parameters>>.sec_sidebolt * 4)
  expr: Constraints[1] = <<Common>>#<<Parameters>>.sec_clampheight / 2
  expr: Constraints[2] = <<Common>>#<<Parameters>>.acc_M4Bore
  sketch-geometry (1):
    g0: Circle CenterX=-74 CenterY=10 CenterZ=0 NormalX=0 NormalY=0 NormalZ=1 AngleXU=0 Radius=2.8
  constraints (3):
    c: DistanceX(g0) = -74
    c: DistanceY(g0) = 10
    c: Diameter(g0) = 5.6
FEATURE [Sketcher::SketchObject] Sketch216  label="LowerClamp_ClampNut_Sketch"
  FullyConstrained = true
  MapMode = 5
  Placement = pos=(103.125,0,0) rot=(0.57735,-0.57735,-0.57735;2.0944rad)
  Support = -> [DatumPlane049]
  expr: Constraints[0] = -<<Common>>#<<Parameters>>.sec_sidebolt_y
  expr: Constraints[1] = <<Common>>#<<Parameters>>.sec_clampheight / 2
  expr: Constraints[2] = <<Common>>#<<Parameters>>.acc_M4Bore
  sketch-geometry (1):
    g0: Circle CenterX=-90 CenterY=10 CenterZ=0 NormalX=0 NormalY=0 NormalZ=1 AngleXU=0 Radius=2.8
  constraints (3):
    c: DistanceX(g0) = -90
    c: DistanceY(g0) = 10
    c: Diameter(g0) = 5.6
FEATURE [Sketcher::SketchObject] Sketch286  label="LowerClamp_ClampBump_Sketch"
  AttachmentOffset = pos=(0,0,10) rot=(0,0,1;0rad)
  ExternalGeometry = -> [ShapeBinder008]
  FullyConstrained = true
  MapMode = 5
  Placement = pos=(0,0,10) rot=(0,0,1;0rad)
  Support = -> [XY_Plane101]
  expr: .AttachmentOffset.Base.z = <<Common>>#<<Parameters>>.sec_stalkheight / 2
  expr: Constraints[54] = <<Common>>#<<Parameters>>.sec_poledia
  sketch-geometry (26):
    g0: LineSegment StartX=107.487 StartY=116.578 StartZ=0 EndX=124.763 EndY=109.422 EndZ=0
    g1: LineSegment StartX=112.547 StartY=121.638 StartZ=0 EndX=119.703 EndY=104.362 EndZ=0
    g2: LineSegment StartX=119.703 StartY=121.638 StartZ=0 EndX=112.547 EndY=104.362 EndZ=0
    g3: LineSegment StartX=124.763 StartY=116.578 StartZ=0 EndX=107.487 EndY=109.422 EndZ=0
    g4: LineSegment StartX=107.487 StartY=116.578 StartZ=0 EndX=112.547 EndY=121.638 EndZ=0
    g5: LineSegment StartX=112.547 StartY=121.638 StartZ=0 EndX=119.703 EndY=121.638 EndZ=0
    g6: LineSegment StartX=119.703 StartY=121.638 StartZ=0 EndX=124.763 EndY=116.578 EndZ=0
    g7: LineSegment StartX=124.763 StartY=116.578 StartZ=0 EndX=124.763 EndY=109.422 EndZ=0
    g8: ArcOfCircle CenterX=119.703 CenterY=104.362 CenterZ=0 NormalX=0 NormalY=0 NormalZ=1 AngleXU=0 Radius=0.35 StartAngle=0.411417 EndAngle=3.51557
    g9: ArcOfCircle CenterX=124.763 CenterY=109.422 CenterZ=0 NormalX=0 NormalY=0 NormalZ=1 AngleXU=0 Radius=0.35 StartAngle=1.19681 EndAngle=4.30097
    g10: ArcOfCircle CenterX=124.763 CenterY=116.578 CenterZ=0 NormalX=0 NormalY=0 NormalZ=1 AngleXU=0 Radius=0.35 StartAngle=1.98221 EndAngle=5.08637
    g11: ArcOfCircle CenterX=119.703 CenterY=121.638 CenterZ=0 NormalX=0 NormalY=0 NormalZ=1 AngleXU=0 Radius=0.35 StartAngle=2.76761 EndAngle=5.87177
    g12: ArcOfCircle CenterX=112.547 CenterY=121.638 CenterZ=0 NormalX=0 NormalY=0 NormalZ=1 AngleXU=0 Radius=0.35 StartAngle=3.55301 EndAngle=6.65717
    g13: ArcOfCircle CenterX=107.487 CenterY=116.578 CenterZ=0 NormalX=0 NormalY=0 NormalZ=1 AngleXU=0 Radius=0.35 StartAngle=4.33841 EndAngle=7.44256
    g14: ArcOfCircle CenterX=107.487 CenterY=109.422 CenterZ=0 NormalX=0 NormalY=0 NormalZ=1 AngleXU=0 Radius=0.35 StartAngle=5.12381 EndAngle=8.22796
    g15: ArcOfCircle CenterX=112.547 CenterY=104.362 CenterZ=0 NormalX=0 NormalY=0 NormalZ=1 AngleXU=0 Radius=0.35 StartAngle=5.9092 EndAngle=9.01336
    g16: ArcOfCircle CenterX=116.125 CenterY=113 CenterZ=0 NormalX=0 NormalY=0 NormalZ=1 AngleXU=0 Radius=9.35 StartAngle=5.06765 EndAngle=5.14252
    g17: ArcOfCircle CenterX=116.125 CenterY=113 CenterZ=0 NormalX=0 NormalY=0 NormalZ=1 AngleXU=0 Radius=9.35 StartAngle=5.85305 EndAngle=5.92792
    g18: ArcOfCircle CenterX=116.125 CenterY=113 CenterZ=0 NormalX=0 NormalY=0 NormalZ=1 AngleXU=0 Radius=9.35 StartAngle=0.355264 EndAngle=0.430134
    g19: ArcOfCircle CenterX=116.125 CenterY=113 CenterZ=0 NormalX=0 NormalY=0 NormalZ=1 AngleXU=0 Radius=9.35 StartAngle=1.14066 EndAngle=1.21553
    g20: ArcOfCircle CenterX=116.125 CenterY=113 CenterZ=0 NormalX=0 NormalY=0 NormalZ=1 AngleXU=0 Radius=9.35 StartAngle=1.92606 EndAngle=2.00093
    g21: ArcOfCircle CenterX=116.125 CenterY=113 CenterZ=0 NormalX=0 NormalY=0 NormalZ=1 AngleXU=0 Radius=9.35 StartAngle=2.71146 EndAngle=2.78633
    g22: ArcOfCircle CenterX=116.125 CenterY=113 CenterZ=0 NormalX=0 NormalY=0 NormalZ=1 AngleXU=0 Radius=9.35 StartAngle=3.49686 EndAngle=3.57173
    g23: ArcOfCircle CenterX=116.125 CenterY=113 CenterZ=0 NormalX=0 NormalY=0 NormalZ=1 AngleXU=0 Radius=9.35 StartAngle=4.28225 EndAngle=4.35713
    g24: GeomPoint X=119.569 Y=104.685 Z=0
    g25: GeomPoint X=112.681 Y=121.315 Z=0
  constraints (76):
    c: Coincident(g4,g0)
    c: Coincident(g5,g1)
    c: Coincident(g6,g2)
    c: Coincident(g7,g3)
    c: Coincident(g4,g1)
    c: Coincident(g5,g2)
    c: Coincident(g6,g3)
    c: Equal(g4,g5)
    c: Equal(g5,g6)
    c: Coincident(g7,g0)
    c: Equal(g7,g5)
    c: Horizontal(g5)
    c: Coincident(g8,g1)
    c: Coincident(g9,g0)
    c: Coincident(g10,g3)
    c: Coincident(g11,g2)
    c: Coincident(g12,g1)
    c: Coincident(g13,g0)
    c: Coincident(g14,g3)
    c: Coincident(g15,g2)
    c: Coincident(g16,g8)
    c: Coincident(g16,g8)
    c: Coincident(g17,g16)
    c: Coincident(g17,g9)
    c: Coincident(g17,g9)
    c: Coincident(g18,g16)
    c: Coincident(g18,g10)
    c: Coincident(g18,g10)
    c: Coincident(g19,g16)
    c: Coincident(g19,g11)
    c: Coincident(g19,g11)
    c: Coincident(g20,g16)
    c: Coincident(g20,g12)
    c: Coincident(g20,g12)
    c: Coincident(g21,g16)
    c: Coincident(g21,g13)
    c: Coincident(g21,g13)
    c: Coincident(g22,g16)
    c: Coincident(g22,g14)
    c: Coincident(g22,g14)
    c: Coincident(g23,g16)
    c: Coincident(g23,g15)
    c: Coincident(g23,g15)
    c: Equal(g8,g9)
    c: Equal(g9,g10)
    c: Equal(g10,g11)
    c: Equal(g11,g12)
    c: Equal(g12,g13)
    c: Equal(g13,g14)
    c: Equal(g14,g15)
    c: PointOnObject(g24,g8)
    c: PointOnObject(g24,g1)
    c: PointOnObject(g25,g12)
    c: PointOnObject(g25,g1)
    c: Distance(g25,g24) = 18
    c: PointOnObject(g16,g0)
    c: PointOnObject(g16,g1)
    c: PointOnObject(g16,g2)
    c: PointOnObject(g16,g3)
    c: PointOnObject(g15,g-3)
    c: PointOnObject(g14,g-3)
    c: PointOnObject(g13,g-3)
    c: PointOnObject(g12,g-3)
    c: PointOnObject(g11,g-3)
    c: PointOnObject(g10,g-3)
    c: PointOnObject(g9,g-3)
    c: PointOnObject(g8,g-3)
    c: PointOnObject(g8,g-3)
    c: PointOnObject(g15,g-3)
    c: PointOnObject(g14,g-3)
    c: PointOnObject(g13,g-3)
    c: PointOnObject(g12,g-3)
    c: PointOnObject(g11,g-3)
    c: PointOnObject(g10,g-3)
    c: PointOnObject(g9,g-3)
    c: Coincident(g16,g-3)
FEATURE [Sketcher::SketchObject] Sketch287  label="LowerClamp_BumpGrad_Sketch"
  AttachmentOffset = pos=(0,0,0) rot=(1,0,0;1.5708rad)
  ExternalGeometry = -> [ShapeBinder008]
  FullyConstrained = true
  MapMode = 11
  Placement = pos=(116.125,113,0) rot=(0.57735,0.57735,0.57735;2.0944rad)
  Support = -> [ShapeBinder008]
  expr: Constraints[21] = <<Common>>#<<Parameters>>.sec_clampheight
  expr: Constraints[23] = <<Common>>#<<Parameters>>.sec_poledia / 2
  expr: Constraints[24] = <<Common>>#<<Parameters>>.sec_clamptol * 5
  sketch-geometry (10):
    g0: LineSegment StartX=0 StartY=0 StartZ=0 EndX=0 EndY=20 EndZ=0
    g1: LineSegment StartX=0 StartY=20 StartZ=0 EndX=9.75 EndY=20 EndZ=0
    g2: LineSegment StartX=0 StartY=0 StartZ=0 EndX=9.75 EndY=0 EndZ=0
    g3: LineSegment StartX=9.75 StartY=20 StartZ=0 EndX=9.35 EndY=19.6 EndZ=0
    g4: LineSegment StartX=9.35 StartY=19.6 StartZ=0 EndX=9.35 EndY=19.2 EndZ=0
    g5: LineSegment StartX=9.35 StartY=19.2 StartZ=0 EndX=9 EndY=15.7 EndZ=0
    g6: LineSegment StartX=9 StartY=15.7 StartZ=0 EndX=9 EndY=4.3 EndZ=0
    g7: LineSegment StartX=9 StartY=4.3 StartZ=0 EndX=9.35 EndY=0.8 EndZ=0
    g8: LineSegment StartX=9.35 StartY=0.8 StartZ=0 EndX=9.35 EndY=0.4 EndZ=0
    g9: LineSegment StartX=9.35 StartY=0.4 StartZ=0 EndX=9.75 EndY=0 EndZ=0
  constraints (29):
    c: Coincident(g0,g-1)
    c: Vertical(g0)
    c: Coincident(g1,g0)
    c: Horizontal(g1)
    c: Coincident(g2,g0)
    c: Horizontal(g2)
    c: Coincident(g3,g1)
    c: Coincident(g4,g3)
    c: Vertical(g4)
    c: Coincident(g5,g4)
    c: Coincident(g6,g5)
    c: Vertical(g6)
    c: Coincident(g7,g6)
    c: Coincident(g8,g7)
    c: Vertical(g8)
    c: Coincident(g9,g8)
    c: Coincident(g9,g2)
    c: Equal(g9,g3)
    c: Equal(g8,g4)
    c: Equal(g5,g7)
    c: Equal(g2,g1)
    c: DistanceY(g0,g0) = 20
    c: DistanceY(g4,g4) = 0.4
    c: DistanceX(g5) = 9
    c: DistanceY(g5,g4) = 3.5
    c: Angle(g1,g3) = 0.785398
    c: DistanceY(g3,g1) = 0.4
    c: PointOnObject(g-3,g8)
    c: PointOnObject(g-3,g4)
FEATURE [PartDesign::Line] DatumLine001  label="LowerClamp_DatumLine_Pole"
  AttacherType = Attacher::AttachEngineLine
  Length = 20
  MapMode = 19
  Placement = pos=(116.125,113,0) rot=(0,0,1;0rad)
  ResizeMode = 0
  Support = -> [ShapeBinder008]
FEATURE [PartDesign::Pad] Pad073  label="LowerClamp_ClampBump"
  BaseFeature = -> Pad057
  Direction = (0,0,1)
  Length = 18.4
  Length2 = 10
  Midplane = true
  Profile = -> Sketch286
  ReferenceAxis = -> Sketch286 [N_Axis]
  Type = 0
  expr: Length = <<Common>>#<<Parameters>>.sec_clampheight - 1.6
FEATURE [PartDesign::Groove] Groove001  label="LowerClamp_BumpGrad"
  Angle = 360
  Axis = (0,0,1)
  Base = (116.125,113,0)
  BaseFeature = -> Pad073
  Profile = -> Sketch287
  ReferenceAxis = -> DatumLine001
FEATURE [PartDesign::Hole] Hole053  label="LowerClamp_ClampNut"
  BaseFeature = -> Groove001
  CustomThreadClearance = 0
  Depth = 141.688
  DepthType = 1
  Diameter = 4.5
  DrillForDepth = false
  DrillPoint = 1
  DrillPointAngle = 118
  HoleCutCountersinkAngle = 90
  HoleCutCustomValues = false
  HoleCutDepth = 4
  HoleCutDiameter = 5.6
  HoleCutType = 1
  ModelThread = false
  Profile = -> Sketch216
  Tapered = false
  TaperedAngle = 90
  ThreadClass = 0
  ThreadDepth = 141.688
  ThreadDepthType = 0
  ThreadDirection = 0
  ThreadFit = 0
  ThreadSize = 11
  ThreadType = 1
  Threaded = false
  UseCustomThreadClearance = false
  expr: HoleCutDiameter = <<Common>>#<<Parameters>>.acc_M4Bore
FEATURE [PartDesign::Hole] Hole054  label="LowerClamp_PlateNut"
  BaseFeature = -> Hole053
  CustomThreadClearance = 0
  Depth = 141.688
  DepthType = 1
  Diameter = 4.5
  DrillForDepth = false
  DrillPoint = 1
  DrillPointAngle = 118
  HoleCutCountersinkAngle = 90
  HoleCutCustomValues = false
  HoleCutDepth = 4
  HoleCutDiameter = 5.6
  HoleCutType = 1
  ModelThread = false
  Profile = -> Sketch215
  Tapered = false
  TaperedAngle = 90
  ThreadClass = 0
  ThreadDepth = 141.688
  ThreadDepthType = 0
  ThreadDirection = 0
  ThreadFit = 0
  ThreadSize = 11
  ThreadType = 1
  Threaded = false
  UseCustomThreadClearance = false
  expr: HoleCutDiameter = <<Common>>#<<Parameters>>.acc_M4Bore
FEATURE [PartDesign::CoordinateSystem] Local_CS270  label="LCS_LowerSideNut"
  AttacherType = Attacher::AttachEngine3D
  MapMode = 11
  Placement = pos=(118.125,74,10) rot=(0.57735,0.57735,-0.57735;4.18879rad)
  Support = -> [Hole054]
FEATURE [PartDesign::CoordinateSystem] Local_CS271  label="LCS_LowerSideBolt"
  AttacherType = Attacher::AttachEngine3D
  AttachmentOffset = pos=(0,0,1) rot=(0,0,1;0rad)
  MapMode = 11
  Placement = pos=(125.125,74,10) rot=(0.57735,-0.57735,0.57735;4.18879rad)
  Support = -> [Hole054]
  expr: .AttachmentOffset.Base.z = <<Common>>#<<Parameters>>.sec_spthick
FEATURE [PartDesign::CoordinateSystem] Local_CS272  label="LCS_LowerClampNut"
  AttacherType = Attacher::AttachEngine3D
  MapMode = 11
  Placement = pos=(103.125,90,10) rot=(0.57735,0.57735,-0.57735;4.18879rad)
  Support = -> [Hole054]
FEATURE [PartDesign::CoordinateSystem] Local_CS273  label="LCS_LowerClampBolt"
  AttacherType = Attacher::AttachEngine3D
  AttachmentOffset = pos=(0,0,1) rot=(0,0,1;0rad)
  MapMode = 11
  Placement = pos=(125.125,90,10) rot=(0.57735,-0.57735,0.57735;4.18879rad)
  Support = -> [Hole054]
  expr: .AttachmentOffset.Base.z = <<Common>>#<<Parameters>>.sec_spthick
FEATURE [PartDesign::CoordinateSystem] Local_CS274  label="LCS_LowerClamp_SidePlate"
  AttacherType = Attacher::AttachEngine3D
  AttachmentOffset = pos=(0,0,0) rot=(0,0,1;3.14159rad)
  MapMode = 11
  Placement = pos=(124.125,90,10) rot=(-0.57735,-0.57735,-0.57735;4.18879rad)
  Support = -> [Hole054]
FEATURE [PartDesign::Chamfer] Chamfer001  label="LowerClamp_Chamfer"
  Angle = 45
  Base = -> Hole054 [Edge84,Edge85,Edge86,Edge87,Edge88,Edge89,Edge90,Edge91,Edge92,Edge93,Edge94,Edge95,Edge63,Edge62,Edge64,Edge65,Edge71,Edge70,Edge72,Edge73,Edge69,Edge68,Edge67,Edge66]
  BaseFeature = -> Hole054
  ChamferType = 0
  FlipDirection = false
  Size = 0.4
  Size2 = 1
  SupportTransform = false
  UseAllEdges = false
FEATURE [PartDesign::Body] Body022048  label="LowerClamp"
  Group = -> [Sketch213,Pad057,DatumPlane049,Sketch214,Sketch215,DatumPlane050,Sketch216,Local_CS270,Local_CS271,Local_CS272,Local_CS273,Local_CS274,ShapeBinder008,Sketch286,Sketch287,DatumLine001,Pad073,Groove001,Hole053,Hole054,Chamfer001]
  Origin = -> Origin102
  Placement = pos=(-3.125,0,781) rot=(0,0,1;0rad)
  Tip = -> Chamfer001
  expr: .Placement.Base.x = -<<Common>>#<<Parameters>>.sec_offset_x
  expr: .Placement.Base.z = <<Common>>#<<Parameters>>.datum_sec_lowerclamp
COMPONENT P3 — recipe-attached ("Shroud", modeled in this document).
Construction recipe (the document's own serialized feature program — sketch geometry with constraints, then the solid features built on it; lengths are millimeters unless a unit is written):

FEATURE [PartDesign::ShapeBinder] ShapeBinder009  label="Shroud_ShapeBinder"
  Support = -> [Binder]
  TraceSupport = false
FEATURE [PartDesign::CoordinateSystem] Local_CS291  label="LCS_Shroud_FarPoleDatum"
  AttacherType = Attacher::AttachEngine3D
  MapMode = 11
  Placement = pos=(-109.875,0,0) rot=(0,0,1;1.5708rad)
  Support = -> [ShapeBinder009]
FEATURE [Sketcher::SketchObject] Sketch217  label="Shroud_Outline_Sketch"
  ExternalGeometry = -> [ShapeBinder009]
  FullyConstrained = true
  MapMode = 5
  Support = -> [XY_Plane103]
  expr: Constraints[13] = 297 / 126 * 1 rad
  sketch-geometry (6):
    g0: LineSegment StartX=3.125 StartY=0 StartZ=0 EndX=3.125 EndY=-126 EndZ=0
    g1: ArcOfCircle CenterX=3.125 CenterY=0 CenterZ=0 NormalX=0 NormalY=0 NormalZ=1 AngleXU=0 Radius=126 StartAngle=1.96302 EndAngle=4.32016
    g2: ArcOfCircle CenterX=3.125 CenterY=0 CenterZ=0 NormalX=0 NormalY=0 NormalZ=1 AngleXU=0 Radius=127 StartAngle=1.96302 EndAngle=4.32016
    g3: LineSegment StartX=-45.4202 StartY=-117.356 StartZ=0 EndX=-45.0379 EndY=-116.432 EndZ=0
    g4: LineSegment StartX=-45.4202 StartY=117.356 StartZ=0 EndX=-45.0379 EndY=116.432 EndZ=0
    g5: LineSegment StartX=-45.0379 StartY=116.432 StartZ=0 EndX=-45.0379 EndY=-116.432 EndZ=0
  constraints (18):
    c: Coincident(g0,g-5)
    c: Vertical(g0)
    c: PointOnObject(g0,g-4)
    c: Coincident(g1,g0)
    c: Coincident(g2,g1)
    c: Coincident(g3,g2)
    c: Coincident(g3,g1)
    c: Perpendicular(g1,g3)
    c: Coincident(g4,g2)
    c: Coincident(g4,g1)
    c: Perpendicular(g1,g4)
    c: Distance(g4) = 1
    c: PointOnObject(g0,g1)
    c: Angle(g4,g3) = 2.35714
    c: DistanceY(g0,g0) = 126  'OuterArc_Rad'
    c: Coincident(g5,g1)
    c: Coincident(g5,g1)
    c: Vertical(g5)
FEATURE [PartDesign::Pad] Pad058  label="Shroud_Base"
  Direction = (0,0,1)
  Length = 210
  Length2 = 10
  Profile = -> Sketch217
  Reversed = true
  Type = 0
FEATURE [PartDesign::Body] Body022050  label="Shroud"
  Group = -> [ShapeBinder009,Local_CS291,Sketch217,Pad058]
  Origin = -> Origin104
  Placement = pos=(-3.125,0,936) rot=(0,0,1;0rad)
  Tip = -> Pad058
  expr: .Placement.Base.x = -<<Common>>#<<Parameters>>.sec_offset_x
  expr: .Placement.Base.z = <<Common>>#<<Parameters>>.datum_sec_upperhub + <<Common>>#<<Parameters>>.sec_stalkheight + <<Common>>#<<Parameters>>.sec_toparc_height + 8
COMPONENT P4 — recipe-attached ("UpperArc", modeled in this document).
Construction recipe (the document's own serialized feature program — sketch geometry with constraints, then the solid features built on it; lengths are millimeters unless a unit is written):

FEATURE [PartDesign::ShapeBinder] ShapeBinder  label="UpperArc_ShapeBinder"
  Support = -> [Binder]
  TraceSupport = false
FEATURE [Sketcher::SketchObject] Sketch297  label="UpperArc_Base_Sketch"
  ExternalGeometry = -> [ShapeBinder]
  FullyConstrained = true
  MapMode = 5
  Support = -> [XY_Plane104]
  expr: Constraints[18] = <<Common>>#<<Parameters>>.sec_fillet * 2
  expr: Constraints[19] = <<Common>>#<<Parameters>>.sec_fthick
  expr: Constraints[55] = <<Common>>#<<Parameters>>.sec_sidebolt * 4
  expr: Constraints[60] = <<Common>>#<<Parameters>>.sec_fthick
  expr: Constraints[63] = <<Common>>#<<Parameters>>.sec_toparc_width
  expr: Constraints[68] = <<Common>>#<<Parameters>>.sec_fthick
  sketch-geometry (29):
    g0: LineSegment StartX=3.125 StartY=126 StartZ=0 EndX=116.125 EndY=126 EndZ=0
    g1: LineSegment StartX=3.125 StartY=118 StartZ=0 EndX=107.692 EndY=118 EndZ=0
    g2: ArcOfCircle CenterX=116.125 CenterY=113 CenterZ=0 NormalX=0 NormalY=0 NormalZ=1 AngleXU=0 Radius=13 StartAngle=3.53638 EndAngle=7.85398
    g3: ArcOfCircle CenterX=116.125 CenterY=113 CenterZ=0 NormalX=0 NormalY=0 NormalZ=1 AngleXU=0 Radius=9.35 StartAngle=3.04482 EndAngle=8.80641
    g4: LineSegment StartX=116.125 StartY=113 StartZ=0 EndX=116.125 EndY=126 EndZ=0
    g5: LineSegment StartX=105.823 StartY=115 StartZ=0 EndX=88.125 EndY=115 EndZ=0
    g6: LineSegment StartX=88.125 StartY=115 StartZ=0 EndX=88.125 EndY=112 EndZ=0
    g7: LineSegment StartX=104.125 StartY=108 StartZ=0 EndX=92.125 EndY=108 EndZ=0
    g8: ArcOfCircle CenterX=92.125 CenterY=112 CenterZ=0 NormalX=0 NormalY=0 NormalZ=1 AngleXU=0 Radius=4 StartAngle=3.14159 EndAngle=4.71239
    g9: LineSegment StartX=88.125 StartY=112 StartZ=0 EndX=92.125 EndY=112 EndZ=0
    g10: LineSegment StartX=92.125 StartY=112 StartZ=0 EndX=92.125 EndY=108 EndZ=0
    g11: LineSegment StartX=3.125 StartY=-126 StartZ=0 EndX=3.125 EndY=126 EndZ=0
    g12: ArcOfCircle CenterX=3.125 CenterY=-3.7e-15 CenterZ=0 NormalX=0 NormalY=0 NormalZ=1 AngleXU=0 Radius=126 StartAngle=1.5708 EndAngle=4.71239
    g13: ArcOfCircle CenterX=3.125 CenterY=-3.7e-15 CenterZ=0 NormalX=0 NormalY=0 NormalZ=1 AngleXU=0 Radius=118 StartAngle=1.5708 EndAngle=4.71239
    g14: ArcOfCircle CenterX=116.125 CenterY=-113 CenterZ=0 NormalX=0 NormalY=0 NormalZ=1 AngleXU=0 Radius=9.35 StartAngle=3.75997 EndAngle=9.52155
    g15: ArcOfCircle CenterX=116.125 CenterY=-113 CenterZ=0 NormalX=0 NormalY=0 NormalZ=1 AngleXU=0 Radius=13 StartAngle=4.71239 EndAngle=9.02999
    g16: LineSegment StartX=3.125 StartY=-126 StartZ=0 EndX=116.125 EndY=-126 EndZ=0
    g17: LineSegment StartX=116.125 StartY=-126 StartZ=0 EndX=116.125 EndY=-113 EndZ=0
    g18: LineSegment StartX=3.125 StartY=-118 StartZ=0 EndX=107.692 EndY=-118 EndZ=0
    g19: LineSegment StartX=104.125 StartY=-108 StartZ=0 EndX=92.125 EndY=-108 EndZ=0
    g20: LineSegment StartX=105.823 StartY=-115 StartZ=0 EndX=88.125 EndY=-115 EndZ=0
    g21: LineSegment StartX=88.125 StartY=-115 StartZ=0 EndX=88.125 EndY=-112 EndZ=0
    g22: ArcOfCircle CenterX=92.125 CenterY=-112 CenterZ=0 NormalX=0 NormalY=0 NormalZ=1 AngleXU=0 Radius=4 StartAngle=1.5708 EndAngle=3.14159
    g23: LineSegment StartX=88.125 StartY=-112 StartZ=0 EndX=92.125 EndY=-112 EndZ=0
    g24: LineSegment StartX=92.125 StartY=-108 StartZ=0 EndX=92.125 EndY=-112 EndZ=0
    g25: ArcOfCircle CenterX=107.692 CenterY=119 CenterZ=0 NormalX=0 NormalY=0 NormalZ=1 AngleXU=0 Radius=1 StartAngle=4.71239 EndAngle=5.66481
    g26: ArcOfCircle CenterX=105.823 CenterY=114 CenterZ=0 NormalX=0 NormalY=0 NormalZ=1 AngleXU=0 Radius=1 StartAngle=6.18642 EndAngle=7.85398
    g27: ArcOfCircle CenterX=105.823 CenterY=-114 CenterZ=0 NormalX=0 NormalY=0 NormalZ=1 AngleXU=0 Radius=1 StartAngle=4.71239 EndAngle=6.37995
    g28: ArcOfCircle CenterX=107.692 CenterY=-119 CenterZ=0 NormalX=0 NormalY=0 NormalZ=1 AngleXU=0 Radius=1 StartAngle=0.618373 EndAngle=1.5708
  constraints (78):
    c: Horizontal(g0)
    c: Horizontal(g1)
    c: Coincident(g3,g2)
    c: Coincident(g4,g2)
    c: Vertical(g4)
    c: Horizontal(g5)
    c: Coincident(g6,g5)
    c: Vertical(g6)
    c: Coincident(g7,g2)
    c: Horizontal(g7)
    c: Coincident(g8,g6)
    c: Coincident(g8,g7)
    c: Coincident(g9,g6)
    c: Coincident(g9,g8)
    c: Coincident(g10,g8)
    c: Coincident(g10,g7)
    c: Vertical(g10)
    c: Horizontal(g9)
    c: Radius(g8) = 4
    c: DistanceY(g6,g6) = 3
    c: Coincident(g4,g0)
    c: Coincident(g2,g0)
    c: Vertical(g11)
    c: Coincident(g11,g0)
    c: PointOnObject(g1,g11)
    c: Coincident(g12,g0)
    c: Coincident(g13,g1)
    c: Coincident(g13,g12)
    c: PointOnObject(g12,g11)
    c: Coincident(g11,g12)
    c: PointOnObject(g13,g11)
    c: Coincident(g15,g14)
    c: Coincident(g16,g12)
    c: Horizontal(g16)
    c: Coincident(g15,g16)
    c: Coincident(g17,g15)
    c: Coincident(g17,g14)
    c: Coincident(g18,g13)
    c: Horizontal(g18)
    c: Coincident(g19,g15)
    c: Horizontal(g19)
    c: Horizontal(g20)
    c: Coincident(g21,g20)
    c: Vertical(g21)
    c: Coincident(g22,g21)
    c: Coincident(g22,g19)
    c: Equal(g8,g22)
    c: Equal(g21,g6)
    c: Equal(g20,g5)
    c: Coincident(g23,g21)
    c: Coincident(g23,g22)
    c: Coincident(g24,g19)
    c: Coincident(g24,g22)
    c: Vertical(g24)
    c: Horizontal(g23)
    c: DistanceX(g6,g2) = 16
    c: Tangent(g3,g25) = 1.5708
    c: Tangent(g1,g25) = -1.5708
    c: Tangent(g5,g26) = -1.5708
    c: Tangent(g3,g26) = 1.5708
    c: DistanceY(g5,g1) = 3
    c: Equal(g26,g25)
    c: Radius(g26) = 1
    c: DistanceY(g1,g0) = 8
    c: Tangent(g20,g27) = 1.5708
    c: Tangent(g14,g27) = 1.5708
    c: Tangent(g18,g28) = 1.5708
    c: Tangent(g14,g28) = 1.5708
    c: DistanceY(g18,g20) = 3
    c: Equal(g27,g28)
    c: Equal(g27,g26)
    c: Coincident(g12,g-3)
    c: Coincident(g2,g-5)
    c: PointOnObject(g3,g-4)
    c: PointOnObject(g0,g-5)
    c: PointOnObject(g14,g-6)
    c: PointOnObject(g15,g-7)
    c: Coincident(g14,g-7)
FEATURE [Sketcher::SketchObject] Sketch298  label="UpperArc_ClampHole_Sketch"
  ExternalGeometry = -> [Sketch297]
  FullyConstrained = true
  MapMode = 5
  Placement = pos=(0,108,0) rot=(1,0,0;1.5708rad)
  expr: Constraints[0] = <<Common>>#<<Parameters>>.sec_sidebolt * 1.1
  expr: Constraints[1] = <<Common>>#<<Parameters>>.sec_toparc_height / 2
  expr: Constraints[2] = <<Common>>#<<Parameters>>.sec_sidebolt * 2
  sketch-geometry (1):
    g0: Circle CenterX=96.125 CenterY=6 CenterZ=0 NormalX=0 NormalY=0 NormalZ=1 AngleXU=0 Radius=2.2
  constraints (3):
    c: Diameter(g0) = 4.4
    c: DistanceY(g0) = 6
    c: DistanceX(g-3,g0) = 8
FEATURE [Sketcher::SketchObject] Sketch299  label="UpperArc_Tab_Sketch"
  AttachmentOffset = pos=(0,0,12) rot=(0,0,1;0rad)
  ExternalGeometry = -> [ShapeBinder]
  FullyConstrained = true
  MapMode = 5
  Placement = pos=(0,0,12) rot=(0,0,1;0rad)
  Support = -> [XY_Plane104]
  expr: .AttachmentOffset.Base.z = <<Common>>#<<Parameters>>.sec_toparc_height
  expr: Constraints[9] = <<Common>>#<<Parameters>>.sec_sidebolt * 3
  sketch-geometry (10):
    g0: ArcOfCircle CenterX=3.125 CenterY=-3.7e-15 CenterZ=0 NormalX=0 NormalY=0 NormalZ=1 AngleXU=0 Radius=126 StartAngle=1.5708 EndAngle=4.71239
    g1: ArcOfCircle CenterX=3.125 CenterY=-3.7e-15 CenterZ=0 NormalX=0 NormalY=0 NormalZ=1 AngleXU=0 Radius=124.4 StartAngle=1.5708 EndAngle=4.71239
    g2: LineSegment StartX=3.125 StartY=126 StartZ=0 EndX=15.125 EndY=126 EndZ=0
    g3: LineSegment StartX=15.125 StartY=126 StartZ=0 EndX=15.125 EndY=124.4 EndZ=0
    g4: LineSegment StartX=15.125 StartY=124.4 StartZ=0 EndX=3.125 EndY=124.4 EndZ=0
    g5: GeomPoint X=-122.875 Y=0 Z=0
    g6: LineSegment StartX=3.125 StartY=126 StartZ=0 EndX=3.125 EndY=-126 EndZ=0
    g7: LineSegment StartX=3.125 StartY=-124.4 StartZ=0 EndX=15.125 EndY=-124.4 EndZ=0
    g8: LineSegment StartX=15.125 StartY=-124.4 StartZ=0 EndX=15.125 EndY=-126 EndZ=0
    g9: LineSegment StartX=15.125 StartY=-126 StartZ=0 EndX=3.125 EndY=-126 EndZ=0
  constraints (28):
    c: Coincident(g1,g0)
    c: DistanceY(g1,g0) = 1.6
    c: Coincident(g2,g0)
    c: Horizontal(g2)
    c: Coincident(g3,g2)
    c: Vertical(g3)
    c: Coincident(g4,g3)
    c: Coincident(g4,g1)
    c: Horizontal(g4)
    c: DistanceX(g2,g2) = 12
    c: PointOnObject(g5,g-1)
    c: PointOnObject(g5,g0)
    c: Coincident(g6,g0)
    c: Vertical(g6)
    c: PointOnObject(g1,g6)
    c: PointOnObject(g1,g6)
    c: Coincident(g0,g6)
    c: PointOnObject(g0,g6)
    c: Coincident(g7,g1)
    c: Horizontal(g7)
    c: Coincident(g8,g7)
    c: Vertical(g8)
    c: Coincident(g9,g8)
    c: Coincident(g9,g0)
    c: Horizontal(g9)
    c: Equal(g7,g4)
    c: Coincident(g0,g-4)
    c: PointOnObject(g5,g-3)
FEATURE [Sketcher::SketchObject] Sketch300  label="UpperArc_Tabcurve_Sketch"
  FullyConstrained = true
  MapMode = 5
  Placement = pos=(0,0,0) rot=(1,0,0;1.5708rad)
  Support = -> [XZ_Plane105]
  expr: Constraints[23] = <<Common>>#<<Parameters>>.sec_offset_x
  expr: Constraints[24] = <<Common>>#<<Parameters>>.sec_stalkheight
  expr: Constraints[25] = <<Common>>#<<Parameters>>.sec_sidebolt * 3
  expr: Constraints[26] = <<Common>>#<<Parameters>>.sec_toparc_height
  sketch-geometry (10):
    g0: ArcOfCircle CenterX=3.125 CenterY=13.5 CenterZ=0 NormalX=0 NormalY=0 NormalZ=1 AngleXU=0 Radius=6.5 StartAngle=0.394791 EndAngle=1.5708
    g1: ArcOfCircle CenterX=15.125 CenterY=18.5 CenterZ=0 NormalX=0 NormalY=0 NormalZ=1 AngleXU=0 Radius=6.5 StartAngle=3.53638 EndAngle=4.71239
    g2: LineSegment StartX=3.125 StartY=13.5 StartZ=0 EndX=15.125 EndY=18.5 EndZ=0
    g3: LineSegment StartX=3.125 StartY=20 StartZ=0 EndX=3.125 EndY=21 EndZ=0
    g4: LineSegment StartX=3.125 StartY=21 StartZ=0 EndX=15.125 EndY=21 EndZ=0
    g5: LineSegment StartX=15.125 StartY=21 StartZ=0 EndX=15.125 EndY=12 EndZ=0
    g6: LineSegment StartX=3.125 StartY=0 StartZ=0 EndX=3.125 EndY=20 EndZ=0
    g7: LineSegment StartX=0 StartY=12 StartZ=0 EndX=15.125 EndY=12 EndZ=0
    g8: LineSegment StartX=15.125 StartY=12 StartZ=0 EndX=15.125 EndY=20 EndZ=0
    g9: LineSegment StartX=15.125 StartY=20 StartZ=0 EndX=3.125 EndY=20 EndZ=0
  constraints (30):
    c: Coincident(g1,g0)
    c: Equal(g1,g0)
    c: Coincident(g2,g0)
    c: Coincident(g2,g1)
    c: PointOnObject(g0,g2)
    c: Coincident(g3,g0)
    c: Vertical(g3)
    c: Coincident(g4,g3)
    c: Horizontal(g4)
    c: Coincident(g5,g4)
    c: Vertical(g5)
    c: DistanceY(g3,g3) = 1
    c: PointOnObject(g6,g-1)
    c: Coincident(g6,g0)
    c: Vertical(g6)
    c: PointOnObject(g7,g-2)
    c: Coincident(g7,g1)
    c: Horizontal(g7)
    c: Coincident(g8,g1)
    c: Vertical(g8)
    c: Coincident(g9,g8)
    c: Coincident(g9,g0)
    c: Horizontal(g9)
    c: DistanceX(g6) = 3.125
    c: DistanceY(g0) = 20
    c: DistanceX(g9,g9) = 12
    c: DistanceY(g7) = 12
    c: PointOnObject(g0,g6)
    c: PointOnObject(g1,g8)
    c: Coincident(g5,g1)
FEATURE [Sketcher::SketchObject] Sketch301  label="UpperArc_Cut"
  ExternalGeometry = -> [ShapeBinder]
  FullyConstrained = true
  MapMode = 5
  Support = -> [XY_Plane104]
  expr: Constraints[17] = <<Common>>#<<Parameters>>.sec_toparc_width
  expr: Constraints[24] = <<Common>>#<<Parameters>>.sec_sidebolt * 4
  expr: Constraints[25] = <<Common>>#<<Parameters>>.sec_toparc_width / 2
  sketch-geometry (14):
    g0: LineSegment StartX=-78.2845 StartY=-101.403 StartZ=0 EndX=-73.2762 EndY=-95.1647 EndZ=0
    g1: LineSegment StartX=-78.2845 StartY=101.403 StartZ=0 EndX=-73.2762 EndY=95.1647 EndZ=0
    g2: LineSegment StartX=-60.1698 StartY=104.342 StartZ=0 EndX=3.125 EndY=0 EndZ=0
    g3: LineSegment StartX=-60.1698 StartY=-104.342 StartZ=0 EndX=3.125 EndY=0 EndZ=0
    g4: ArcOfCircle CenterX=3.125 CenterY=0 CenterZ=0 NormalX=0 NormalY=0 NormalZ=1 AngleXU=0 Radius=122.039 StartAngle=2.11606 EndAngle=2.24726
    g5: ArcOfCircle CenterX=3.125 CenterY=0 CenterZ=0 NormalX=0 NormalY=0 NormalZ=1 AngleXU=0 Radius=122.039 StartAngle=4.03592 EndAngle=4.16712
    g6: ArcOfCircle CenterX=3.125 CenterY=0 CenterZ=0 NormalX=0 NormalY=0 NormalZ=1 AngleXU=0 Radius=126.039 StartAngle=1.59559 EndAngle=4.68759
    g7: LineSegment StartX=-4.9e-15 StartY=126 StartZ=0 EndX=116.125 EndY=126 EndZ=0
    g8: LineSegment StartX=116.125 StartY=126 StartZ=0 EndX=116.125 EndY=113 EndZ=0
    g9: LineSegment StartX=-73.2762 StartY=95.1647 StartZ=0 EndX=-62.8363 EndY=94.2025 EndZ=0
    g10: LineSegment StartX=-60.1698 StartY=104.342 StartZ=0 EndX=-62.8363 EndY=94.2025 EndZ=0
    g11: GeomPoint X=-75.7804 Y=98.2838 Z=0
    g12: LineSegment StartX=-73.2762 StartY=-95.1647 StartZ=0 EndX=-62.8363 EndY=-94.2025 EndZ=0
    g13: LineSegment StartX=-62.8363 StartY=-94.2025 StartZ=0 EndX=-60.1698 EndY=-104.342 EndZ=0
  constraints (37):
    c: Coincident(g2,g3)
    c: Coincident(g4,g2)
    c: Coincident(g4,g2)
    c: Coincident(g4,g1)
    c: Coincident(g5,g2)
    c: Coincident(g5,g3)
    c: Coincident(g5,g0)
    c: Coincident(g6,g2)
    c: PointOnObject(g7,g-2)
    c: Horizontal(g7)
    c: Coincident(g6,g7)
    c: Coincident(g8,g7)
    c: Vertical(g8)
    c: PointOnObject(g6,g-2)
    c: PointOnObject(g2,g1)
    c: PointOnObject(g2,g0)
    c: Equal(g0,g1)
    c: Distance(g1) = 8
    c: Coincident(g9,g1)
    c: Coincident(g10,g2)
    c: Coincident(g10,g9)
    c: Equal(g9,g10)
    c: PointOnObject(g11,g1)
    c: PointOnObject(g11,g6)
    c: Distance(g1,g2) = 16
    c: Distance(g11,g1) = 4
    c: Coincident(g12,g0)
    c: Coincident(g13,g12)
    c: Coincident(g13,g3)
    c: Equal(g13,g12)
    c: Equal(g13,g9)
    c: Equal(g2,g3)
    c: PointOnObject(g7,g-5)
    c: Coincident(g9,g-3)
    c: Coincident(g12,g-4)
    c: Coincident(g2,g-4)
    c: Coincident(g8,g-5)
FEATURE [PartDesign::Pad] Pad074  label="UpperArc_Base"
  Direction = (0,0,1)
  Length = 12
  Length2 = 10
  Profile = -> Sketch297
  ReferenceAxis = -> Sketch297 [N_Axis]
  Type = 0
  expr: Length = <<Common>>#<<Parameters>>.sec_toparc_height
FEATURE [PartDesign::Pad] Pad075  label="UpperArc_Tab"
  BaseFeature = -> Pad074
  Direction = (0,0,1)
  Length = 8
  Length2 = 10
  Profile = -> Sketch299
  ReferenceAxis = -> Sketch299 [N_Axis]
  Type = 0
  expr: Length = <<Common>>#<<Parameters>>.sec_stalkheight - <<Common>>#<<Parameters>>.sec_toparc_height
FEATURE [PartDesign::Pocket] Pocket001  label="UpperArc_Tabcurve"
  BaseFeature = -> Pad075
  Direction = (0,1,2e-16)
  Length = 5
  Length2 = 5
  Midplane = true
  Profile = -> Sketch300
  ReferenceAxis = -> Sketch300 [N_Axis]
  Type = 1
FEATURE [PartDesign::Hole] Hole055  label="UpperArc_ClampHole"
  BaseFeature = -> Pocket001
  CustomThreadClearance = 0
  Depth = 720.915
  DepthType = 1
  Diameter = 4.5
  DrillForDepth = false
  DrillPoint = 1
  DrillPointAngle = 118
  HoleCutCountersinkAngle = 90
  HoleCutCustomValues = false
  HoleCutDepth = 4
  HoleCutDiameter = 5.6
  HoleCutType = 1
  ModelThread = false
  Profile = -> Sketch298
  Tapered = false
  TaperedAngle = 90
  ThreadClass = 0
  ThreadDepth = 720.915
  ThreadDepthType = 0
  ThreadDirection = 0
  ThreadFit = 0
  ThreadSize = 11
  ThreadType = 1
  Threaded = false
  UseCustomThreadClearance = false
  expr: HoleCutDiameter = <<Common>>#<<Parameters>>.acc_M4Bore
FEATURE [PartDesign::Mirrored] Mirrored  label="UpperArc_Mirrored"
  BaseFeature = -> Hole055
  MirrorPlane = -> XZ_Plane105
  Originals = -> [Hole055]
FEATURE [PartDesign::CoordinateSystem] Local_CS  label="LCS_UpperArc_ClampNut_A"
  AttacherType = Attacher::AttachEngine3D
  MapMode = 11
  Placement = pos=(96.125,108,6) rot=(0.57735,0.57735,-0.57735;2.0944rad)
  Support = -> [Mirrored]
FEATURE [PartDesign::CoordinateSystem] Local_CS292  label="LCS_UpperArc_ClampBolt_A"
  AttacherType = Attacher::AttachEngine3D
  MapMode = 11
  Placement = pos=(96.125,126,6) rot=(0.57735,0.57735,0.57735;4.18879rad)
  Support = -> [Mirrored]
FEATURE [PartDesign::CoordinateSystem] Local_CS293  label="LCS_UpperArc_ClampNut_F"
  AttacherType = Attacher::AttachEngine3D
  MapMode = 11
  Placement = pos=(96.125,-108,6) rot=(-0.57735,-0.57735,-0.57735;2.0944rad)
  Support = -> [Mirrored]
FEATURE [PartDesign::CoordinateSystem] Local_CS294  label="LCS_UpperArc_ClampBolt_F"
  AttacherType = Attacher::AttachEngine3D
  MapMode = 11
  Placement = pos=(96.125,-126,6) rot=(0.57735,0.57735,-0.57735;2.0944rad)
  Support = -> [Mirrored]
FEATURE [PartDesign::CoordinateSystem] Local_CS295  label="LCS_UpperArc_Pole_A"
  AttacherType = Attacher::AttachEngine3D
  MapMode = 11
  Placement = pos=(116.125,113,0) rot=(0,0,1;1.5708rad)
  Support = -> [ShapeBinder]
FEATURE [PartDesign::CoordinateSystem] Local_CS296  label="LCS_UpperArc_FarPoleDatum"
  AttacherType = Attacher::AttachEngine3D
  MapMode = 11
  Placement = pos=(-109.875,0,0) rot=(0,0,1;1.5708rad)
  Support = -> [ShapeBinder]
FEATURE [PartDesign::Chamfer] Chamfer002  label="UpperArc_Chamfer"
  Angle = 45
  Base = -> Mirrored [Face3]
  BaseFeature = -> Mirrored
  ChamferType = 0
  FlipDirection = false
  Size = 0.4
  Size2 = 1
  SupportTransform = false
  UseAllEdges = false
FEATURE [PartDesign::Body] Body022052  label="UpperArc"
  Group = -> [ShapeBinder,Sketch297,Sketch298,Sketch299,Sketch300,Sketch301,Pad074,Pad075,Pocket001,Hole055,Mirrored,Local_CS,Local_CS292,Local_CS293,Local_CS294,Local_CS295,Local_CS296,Chamfer002]
  Origin = -> Origin106
  Placement = pos=(-3.125,0,916) rot=(0,0,1;0rad)
  Tip = -> Chamfer002
  expr: .Placement.Base.x = -<<Common>>#<<Parameters>>.sec_offset_x
  expr: .Placement.Base.z = <<Common>>#<<Parameters>>.datum_sec_upperhub + <<Common>>#<<Parameters>>.sec_stalkheight
COMPONENT P5 — recipe-attached ("MirrorCover_500", modeled in this document).
Construction recipe (the document's own serialized feature program — sketch geometry with constraints, then the solid features built on it; lengths are millimeters unless a unit is written):

FEATURE [PartDesign::ShapeBinder] ShapeBinder010  label="MirrorCover500_ShapeBinder_Spider"
  Support = -> [Binder]
  TraceSupport = false
FEATURE [Sketcher::SketchObject] Sketch302
  FullyConstrained = true
  MapMode = 5
  Placement = pos=(0,0,0) rot=(1,0,0;1.5708rad)
  Support = -> [XZ_Plane107]
  sketch-geometry (13):
    g0: LineSegment StartX=28 StartY=0.6 StartZ=0 EndX=28 EndY=110.443 EndZ=0
    g1: LineSegment StartX=28 StartY=110.443 StartZ=0 EndX=29.2 EndY=110.443 EndZ=0
    g2: LineSegment StartX=0 StartY=-1.2 StartZ=0 EndX=0 EndY=0 EndZ=0
    g3: LineSegment StartX=29.2 StartY=110.443 StartZ=0 EndX=29.2 EndY=108.443 EndZ=0
    g4: LineSegment StartX=29.2 StartY=105 StartZ=0 EndX=29.2 EndY=-0.6 EndZ=0
    g5: LineSegment StartX=0 StartY=0 StartZ=0 EndX=27.4 EndY=0 EndZ=0
    g6: LineSegment StartX=27.4 StartY=0 StartZ=0 EndX=28 EndY=0.6 EndZ=0
    g7: LineSegment StartX=29.2 StartY=-0.6 StartZ=0 EndX=28.6 EndY=-1.2 EndZ=0
    g8: LineSegment StartX=28.6 StartY=-1.2 StartZ=0 EndX=0 EndY=-1.2 EndZ=0
    g9: LineSegment StartX=29.2 StartY=108.443 StartZ=0 EndX=29.6454 EndY=107.672 EndZ=0
    g10: LineSegment StartX=29.2 StartY=105 StartZ=0 EndX=29.6454 EndY=105.772 EndZ=0
    g11: ArcOfCircle CenterX=28 CenterY=106.722 CenterZ=0 NormalX=0 NormalY=0 NormalZ=1 AngleXU=0 Radius=1.9 StartAngle=5.75959 EndAngle=6.80678
    g12: LineSegment StartX=28 StartY=106.722 StartZ=0 EndX=29.9 EndY=106.722 EndZ=0
  constraints (38):
    c: Coincident(g5,g-1)
    c: Coincident(g0,g6)
    c: Vertical(g0)
    c: Coincident(g1,g0)
    c: Horizontal(g1)
    c: Coincident(g3,g1)
    c: Coincident(g7,g4)
    c: Coincident(g2,g8)
    c: Coincident(g2,g5)
    c: Vertical(g2)
    c: Equal(g2,g1)
    c: DistanceY(g2,g2) = 1.2
    c: DistanceX(g0) = 28
    c: Vertical(g3)
    c: Vertical(g4)
    c: DistanceY(g3,g3) = 2
    c: PointOnObject(g4,g3)
    c: DistanceY(g4) = 105
    c: Coincident(g5,g6)
    c: Horizontal(g5)
    c: Coincident(g7,g8)
    c: Horizontal(g8)
    c: Angle(g0,g6) = 2.35619
    c: Parallel(g7,g6)
    c: Equal(g7,g6)
    c: DistanceY(g7,g4) = 0.6
    c: Coincident(g9,g3)
    c: Coincident(g10,g4)
    c: Angle(g4,g10) = 2.61799
    c: Angle(g9,g3) = 2.61799
    c: PointOnObject(g11,g0)
    c: Coincident(g12,g11)
    c: PointOnObject(g12,g11)
    c: Horizontal(g12)
    c: DistanceX(g1,g12) = 0.7
    c: Tangent(g11,g9) = 1.5708
    c: Tangent(g11,g10) = -1.5708
    c: DistanceX(g12) = 29.9
FEATURE [PartDesign::Revolution] Revolution
  Angle = 360
  Axis = (1e-16,1e-16,1)
  Base = (0,0,0)
  Placement = pos=(0,0,0) rot=(1,0,0;1.5708rad)
  Profile = -> Sketch302
  ReferenceAxis = -> Z_Axis107
FEATURE [Sketcher::SketchObject] Sketch303
  AttachmentOffset = pos=(0,0,75) rot=(0,0,1;0rad)
  ExternalGeometry = -> [ShapeBinder010,Revolution]
  FullyConstrained = true
  MapMode = 5
  Placement = pos=(0,0,75) rot=(0,0,1;0rad)
  Support = -> [XY_Plane106]
  sketch-geometry (20):
    g0: LineSegment StartX=5.49564 StartY=32.0691 StartZ=0 EndX=7.61696 EndY=29.9478 EndZ=0
    g1: LineSegment StartX=7.61696 StartY=29.9478 StartZ=0 EndX=3.51322 EndY=25.8441 EndZ=0
    g2: LineSegment StartX=3.51322 StartY=25.8441 StartZ=0 EndX=1.3919 EndY=27.9654 EndZ=0
    g3: LineSegment StartX=1.3919 StartY=27.9654 StartZ=0 EndX=5.49564 EndY=32.0691 EndZ=0
    g4: LineSegment StartX=5.49564 StartY=-32.0691 StartZ=0 EndX=7.61696 EndY=-29.9478 EndZ=0
    g5: LineSegment StartX=7.61696 StartY=-29.9478 StartZ=0 EndX=3.51322 EndY=-25.8441 EndZ=0
    g6: LineSegment StartX=3.51322 StartY=-25.8441 StartZ=0 EndX=1.3919 EndY=-27.9654 EndZ=0
    g7: LineSegment StartX=1.3919 StartY=-27.9654 StartZ=0 EndX=5.49564 EndY=-32.0691 EndZ=0
    g8: LineSegment StartX=2.51777 StartY=29.0913 StartZ=0 EndX=4.63909 EndY=26.9699 EndZ=0
    g9: GeomPoint X=3.93198 Y=27.677 Z=0
    g10: LineSegment StartX=2.51777 StartY=-29.0913 StartZ=0 EndX=4.63909 EndY=-26.9699 EndZ=0
    g11: GeomPoint X=3.93198 Y=-27.677 Z=0
    g12: LineSegment StartX=-31.2 StartY=1 StartZ=0 EndX=31.2 EndY=1 EndZ=0
    g13: LineSegment StartX=31.2 StartY=1 StartZ=0 EndX=31.2 EndY=-1 EndZ=0
    g14: LineSegment StartX=31.2 StartY=-1 StartZ=0 EndX=-31.2 EndY=-1 EndZ=0
    g15: LineSegment StartX=-31.2 StartY=-1 StartZ=0 EndX=-31.2 EndY=1 EndZ=0
    g16: GeomPoint X=-29.2 Y=0 Z=0
    g17: GeomPoint X=29.2 Y=0 Z=0
    g18: GeomPoint X=6.20275 Y=28.5336 Z=0
    g19: GeomPoint X=6.20275 Y=-28.5336 Z=0
  constraints (55):
    c: Coincident(g0,g1)
    c: Coincident(g1,g2)
    c: Coincident(g2,g3)
    c: Coincident(g3,g0)
    c: Coincident(g4,g5)
    c: Coincident(g5,g6)
    c: Coincident(g6,g7)
    c: Coincident(g7,g4)
    c: Perpendicular(g-3,g0)
    c: Perpendicular(g-3,g2)
    c: Parallel(g1,g3)
    c: Parallel(g-3,g3)
    c: Parallel(g5,g7)
    c: Parallel(g7,g-4)
    c: Parallel(g4,g6)
    c: PointOnObject(g8,g3)
    c: PointOnObject(g8,g1)
    c: Perpendicular(g-3,g8)
    c: PointOnObject(g9,g8)
    c: PointOnObject(g9,g-3)
    c: Distance(g8,g9) = 1
    c: Distance(g8,g9) = 2
    c: Perpendicular(g-4,g6)
    c: PointOnObject(g10,g5)
    c: Perpendicular(g-4,g10)
    c: PointOnObject(g11,g10)
    c: PointOnObject(g11,g-4)
    c: Distance(g10,g11) = 1
    c: Distance(g10,g11) = 2
    c: Coincident(g12,g13)
    c: Coincident(g13,g14)
    c: Coincident(g14,g15)
    c: Coincident(g15,g12)
    c: Horizontal(g12)
    c: Horizontal(g14)
    c: Vertical(g13)
    c: Symmetric(g12,g14,g-1)
    c: DistanceY(g13,g13) = 2
    c: PointOnObject(g16,g-6)
    c: PointOnObject(g17,g-1)
    c: PointOnObject(g17,g-6)
    c: DistanceX(g17,g12) = 2
    c: DistanceX(g12,g16) = 2
    c: PointOnObject(g16,g-1)
    c: PointOnObject(g2,g-5)
    c: PointOnObject(g8,g-6)
    c: PointOnObject(g18,g-6)
    c: PointOnObject(g18,g1)
    c: Distance(g18,g0) = 2
    c: PointOnObject(g6,g-5)
    c: PointOnObject(g10,g7)
    c: PointOnObject(g10,g-6)
    c: PointOnObject(g19,g5)
    c: PointOnObject(g19,g-6)
    c: Distance(g19,g4) = 2
FEATURE [PartDesign::Pocket] Pocket002
  BaseFeature = -> Revolution
  Direction = (0,0,-1)
  Length = 5
  Length2 = 5
  Placement = pos=(0,0,0) rot=(1,0,0;1.5708rad)
  Profile = -> Sketch303
  ReferenceAxis = -> Sketch303 [N_Axis]
  Reversed = true
  Type = 1
FEATURE [PartDesign::Body] Body022053  label="MirrorCover_500"
  Group = -> [ShapeBinder010,Sketch302,Revolution,Sketch303,Pocket002]
  Origin = -> Origin108
  Tip = -> Pocket002
COMPONENT P6 — recipe-attached ("MirrorCoverCap_500", modeled in this document).
Construction recipe (the document's own serialized feature program — sketch geometry with constraints, then the solid features built on it; lengths are millimeters unless a unit is written):

FEATURE [Sketcher::SketchObject] Sketch304
  FullyConstrained = true
  MapMode = 5
  Placement = pos=(0,0,0) rot=(1,0,0;1.5708rad)
  Support = -> [XZ_Plane108]
  sketch-geometry (12):
    g0: LineSegment StartX=29.9 StartY=8.20854 StartZ=0 EndX=31.1 EndY=8.20854 EndZ=0
    g1: LineSegment StartX=31.1 StartY=8.20854 StartZ=0 EndX=31.1 EndY=-0.6 EndZ=0
    g2: LineSegment StartX=8.5 StartY=-1.2 StartZ=0 EndX=8.5 EndY=0 EndZ=0
    g3: LineSegment StartX=29.7565 StartY=8.06504 StartZ=0 EndX=29.9 EndY=8.20854 EndZ=0
    g4: LineSegment StartX=29.9 StartY=0.6 StartZ=0 EndX=29.9 EndY=5 EndZ=0
    g5: LineSegment StartX=29.9 StartY=5 StartZ=0 EndX=29.4546 EndY=5.77154 EndZ=0
    g6: LineSegment StartX=8.5 StartY=0 StartZ=0 EndX=29.3 EndY=0 EndZ=0
    g7: LineSegment StartX=29.3 StartY=0 StartZ=0 EndX=29.9 EndY=0.6 EndZ=0
    g8: LineSegment StartX=31.1 StartY=-0.6 StartZ=0 EndX=30.5 EndY=-1.2 EndZ=0
    g9: LineSegment StartX=30.5 StartY=-1.2 StartZ=0 EndX=8.5 EndY=-1.2 EndZ=0
    g10: LineSegment StartX=31.1 StartY=6.72154 StartZ=0 EndX=29.2 EndY=6.72154 EndZ=0
    g11: ArcOfCircle CenterX=31.1 CenterY=6.72154 CenterZ=0 NormalX=0 NormalY=0 NormalZ=1 AngleXU=0 Radius=1.9 StartAngle=2.35619 EndAngle=3.66519
  constraints (35):
    c: PointOnObject(g6,g-1)
    c: Coincident(g4,g7)
    c: Coincident(g0,g3)
    c: Coincident(g1,g0)
    c: Vertical(g1)
    c: Coincident(g8,g1)
    c: Coincident(g2,g9)
    c: Coincident(g2,g6)
    c: Horizontal(g0)
    c: Vertical(g2)
    c: Equal(g2,g0)
    c: DistanceY(g2,g2) = 1.2
    c: DistanceX(g9) = 8.5
    c: Coincident(g4,g5)
    c: Vertical(g4)
    c: PointOnObject(g0,g4)
    c: Coincident(g6,g7)
    c: Horizontal(g6)
    c: Coincident(g8,g9)
    c: Horizontal(g9)
    c: DistanceY(g6,g4) = 5
    c: Equal(g8,g7)
    c: Parallel(g8,g7)
    c: Angle(g4,g7) = 2.35619
    c: DistanceY(g8,g1) = 0.6
    c: PointOnObject(g10,g1)
    c: Horizontal(g10)
    c: Coincident(g11,g10)
    c: PointOnObject(g10,g11)
    c: Tangent(g11,g5) = 1.5708
    c: DistanceX(g10) = 29.2
    c: Tangent(g11,g3) = 1.5708
    c: Angle(g3,g0) = 2.35619
    c: DistanceX(g10,g0) = 0.7
    c: Angle(g5,g4) = 2.61799
FEATURE [PartDesign::Revolution] Revolution001
  Angle = 360
  Axis = (1e-16,1e-16,1)
  Base = (0,0,0)
  Placement = pos=(0,0,0) rot=(1,0,0;1.5708rad)
  Profile = -> Sketch304
  ReferenceAxis = -> Z_Axis108
  Reversed = true
FEATURE [Sketcher::SketchObject] Sketch309
  AttachmentOffset = pos=(0,0,5) rot=(0,0,1;0rad)
  ExternalGeometry = -> [Revolution001]
  FullyConstrained = true
  MapMode = 5
  Placement = pos=(0,0,5) rot=(0,0,1;0rad)
  Support = -> [XY_Plane107]
  sketch-geometry (17):
    g0: ArcOfCircle CenterX=1e-16 CenterY=1e-16 CenterZ=0 NormalX=0 NormalY=0 NormalZ=1 AngleXU=0 Radius=29.9 StartAngle=0.392699 EndAngle=1.1781
    g1: LineSegment StartX=27.624 StartY=11.4422 StartZ=0 EndX=16.1818 EndY=0 EndZ=0
    g2: LineSegment StartX=16.1818 StartY=0 StartZ=0 EndX=27.624 EndY=-11.4422 EndZ=0
    g3: ArcOfCircle CenterX=1e-16 CenterY=1e-16 CenterZ=0 NormalX=0 NormalY=0 NormalZ=1 AngleXU=0 Radius=29.9 StartAngle=5.10509 EndAngle=5.89049
    g4: LineSegment StartX=11.4422 StartY=-27.624 StartZ=0 EndX=0 EndY=-16.1818 EndZ=0
    g5: LineSegment StartX=0 StartY=-16.1818 StartZ=0 EndX=-11.4422 EndY=-27.624 EndZ=0
    g6: ArcOfCircle CenterX=1e-16 CenterY=1e-16 CenterZ=0 NormalX=0 NormalY=0 NormalZ=1 AngleXU=0 Radius=29.9 StartAngle=3.53429 EndAngle=4.31969
    g7: LineSegment StartX=-27.624 StartY=-11.4422 StartZ=0 EndX=-16.1818 EndY=0 EndZ=0
    g8: LineSegment StartX=-16.1818 StartY=0 StartZ=0 EndX=-27.624 EndY=11.4422 EndZ=0
    g9: ArcOfCircle CenterX=1e-16 CenterY=1e-16 CenterZ=0 NormalX=0 NormalY=0 NormalZ=1 AngleXU=0 Radius=29.9 StartAngle=1.9635 EndAngle=2.74889
    g10: LineSegment StartX=-11.4422 StartY=27.624 StartZ=0 EndX=0 EndY=16.1818 EndZ=0
    g11: LineSegment StartX=0 StartY=16.1818 StartZ=0 EndX=11.4422 EndY=27.624 EndZ=0
    g12: LineSegment StartX=-11.4422 StartY=27.624 StartZ=0 EndX=11.4422 EndY=27.624 EndZ=0
    g13: LineSegment StartX=27.624 StartY=11.4422 StartZ=0 EndX=27.624 EndY=-11.4422 EndZ=0
    g14: LineSegment StartX=11.4422 StartY=-27.624 StartZ=0 EndX=-11.4422 EndY=-27.624 EndZ=0
    g15: LineSegment StartX=-27.624 StartY=-11.4422 StartZ=0 EndX=-27.624 EndY=11.4422 EndZ=0
    g16: LineSegment StartX=-27.624 StartY=11.4422 StartZ=0 EndX=-11.4422 EndY=27.624 EndZ=0
  constraints (46):
    c: Coincident(g1,g0)
    c: Perpendicular(g1,g2)
    c: Coincident(g2,g1)
    c: Equal(g2,g1)
    c: Coincident(g3,g0)
    c: Coincident(g3,g2)
    c: Coincident(g4,g3)
    c: Coincident(g5,g4)
    c: Coincident(g6,g0)
    c: Coincident(g6,g5)
    c: Coincident(g7,g6)
    c: Coincident(g8,g7)
    c: Coincident(g9,g0)
    c: Coincident(g9,g8)
    c: Coincident(g10,g9)
    c: Coincident(g11,g10)
    c: Coincident(g11,g0)
    c: Coincident(g12,g9)
    c: Coincident(g12,g0)
    c: Coincident(g13,g0)
    c: Coincident(g13,g2)
    c: Coincident(g14,g3)
    c: Coincident(g14,g5)
    c: Coincident(g15,g6)
    c: Coincident(g15,g8)
    c: Equal(g14,g15)
    c: Equal(g15,g13)
    c: Equal(g13,g12)
    c: Equal(g11,g10)
    c: Equal(g8,g7)
    c: Equal(g5,g4)
    c: Equal(g2,g5)
    c: Equal(g5,g8)
    c: Equal(g8,g11)
    c: PointOnObject(g10,g-2)
    c: PointOnObject(g7,g-1)
    c: PointOnObject(g1,g-1)
    c: PointOnObject(g4,g-2)
    c: Coincident(g16,g8)
    c: Coincident(g16,g9)
    c: Equal(g16,g12)
    c: PointOnObject(g2,g-3)
    c: PointOnObject(g5,g-3)
    c: PointOnObject(g8,g-3)
    c: PointOnObject(g0,g-3)
    c: Coincident(g0,g-3)
FEATURE [PartDesign::Pocket] Pocket005
  BaseFeature = -> Revolution001
  Direction = (0,0,-1)
  Length = 5
  Length2 = 5
  Placement = pos=(0,0,0) rot=(1,0,0;1.5708rad)
  Profile = -> Sketch309
  ReferenceAxis = -> Sketch309 [N_Axis]
  Reversed = true
  Type = 1
FEATURE [PartDesign::Body] Body022054  label="MirrorCoverCap_500"
  Group = -> [Sketch304,Revolution001,Sketch309,Pocket005]
  Origin = -> Origin109
  Tip = -> Pocket005
COMPONENT P7 — recipe-attached ("MirrorCover_625", modeled in this document).
Construction recipe (the document's own serialized feature program — sketch geometry with constraints, then the solid features built on it; lengths are millimeters unless a unit is written):

FEATURE [PartDesign::ShapeBinder] ShapeBinder011  label="MirrorCover625_ShapeBinder_Spider"
  Support = -> [Binder]
  TraceSupport = false
FEATURE [Sketcher::SketchObject] Sketch305
  FullyConstrained = true
  MapMode = 5
  Placement = pos=(0,0,0) rot=(1,0,0;1.5708rad)
  Support = -> [XZ_Plane107]
  sketch-geometry (12):
    g0: LineSegment StartX=40 StartY=0.6 StartZ=0 EndX=40 EndY=132 EndZ=0
    g1: LineSegment StartX=40 StartY=132 StartZ=0 EndX=41.2 EndY=132 EndZ=0
    g2: LineSegment StartX=0 StartY=-1.2 StartZ=0 EndX=0 EndY=0 EndZ=0
    g3: LineSegment StartX=41.2 StartY=132 StartZ=0 EndX=41.2 EndY=130 EndZ=0
    g4: LineSegment StartX=41.2 StartY=130 StartZ=0 EndX=41.9 EndY=128.5 EndZ=0
    g5: LineSegment StartX=41.9 StartY=128.5 StartZ=0 EndX=41.9 EndY=126.5 EndZ=0
    g6: LineSegment StartX=41.9 StartY=126.5 StartZ=0 EndX=41.2 EndY=125 EndZ=0
    g7: LineSegment StartX=41.2 StartY=125 StartZ=0 EndX=41.2 EndY=-0.6 EndZ=0
    g8: LineSegment StartX=0 StartY=0 StartZ=0 EndX=39.4 EndY=0 EndZ=0
    g9: LineSegment StartX=39.4 StartY=0 StartZ=0 EndX=40 EndY=0.6 EndZ=0
    g10: LineSegment StartX=41.2 StartY=-0.6 StartZ=0 EndX=40.6 EndY=-1.2 EndZ=0
    g11: LineSegment StartX=40.6 StartY=-1.2 StartZ=0 EndX=0 EndY=-1.2 EndZ=0
  constraints (36):
    c: Coincident(g8,g-1)
    c: Coincident(g0,g9)
    c: Vertical(g0)
    c: Coincident(g1,g0)
    c: Horizontal(g1)
    c: Coincident(g3,g1)
    c: Coincident(g10,g7)
    c: Coincident(g2,g11)
    c: Coincident(g2,g8)
    c: Vertical(g2)
    c: DistanceY(g2,g2) = 1.2
    c: DistanceX(g0) = 40
    c: Coincident(g3,g4)
    c: Vertical(g3)
    c: Coincident(g4,g5)
    c: Coincident(g5,g6)
    c: Vertical(g5)
    c: Coincident(g6,g7)
    c: Vertical(g7)
    c: DistanceY(g5,g5) = 2
    c: Equal(g4,g6)
    c: DistanceY(g3,g3) = 2
    c: PointOnObject(g6,g3)
    c: DistanceX(g3,g4) = 0.7
    c: DistanceY(g6,g5) = 1.5
    c: DistanceY(g6) = 125
    c: DistanceX(g5) = 41.9
    c: Equal(g1,g2)
    c: Coincident(g8,g9)
    c: Horizontal(g8)
    c: Coincident(g10,g11)
    c: Horizontal(g11)
    c: Angle(g0,g9) = 2.35619
    c: Parallel(g10,g9)
    c: DistanceY(g10,g7) = 0.6
    c: Equal(g9,g10)
FEATURE [PartDesign::Revolution] Revolution002
  Angle = 360
  Axis = (1e-16,1e-16,1)
  Base = (0,0,0)
  Placement = pos=(0,0,0) rot=(1,0,0;1.5708rad)
  Profile = -> Sketch305
  ReferenceAxis = -> Z_Axis107
FEATURE [Sketcher::SketchObject] Sketch306
  AttachmentOffset = pos=(0,0,95) rot=(0,0,1;0rad)
  ExternalGeometry = -> [ShapeBinder011,Revolution002]
  FullyConstrained = true
  MapMode = 5
  Placement = pos=(0,0,95) rot=(0,0,1;0rad)
  Support = -> [XY_Plane106]
  sketch-geometry (18):
    g0: LineSegment StartX=14.1566 StartY=40.7301 StartZ=0 EndX=16.2779 EndY=38.6088 EndZ=0
    g1: LineSegment StartX=16.2779 StartY=38.6088 StartZ=0 EndX=13.8038 EndY=36.1347 EndZ=0
    g2: LineSegment StartX=13.8038 StartY=36.1347 StartZ=0 EndX=11.6825 EndY=38.256 EndZ=0
    g3: LineSegment StartX=11.6825 StartY=38.256 StartZ=0 EndX=14.1566 EndY=40.7301 EndZ=0
    g4: LineSegment StartX=14.1566 StartY=-40.7301 StartZ=0 EndX=16.2779 EndY=-38.6088 EndZ=0
    g5: LineSegment StartX=16.2779 StartY=-38.6088 StartZ=0 EndX=13.8038 EndY=-36.1347 EndZ=0
    g6: LineSegment StartX=13.8038 StartY=-36.1347 StartZ=0 EndX=11.6825 EndY=-38.256 EndZ=0
    g7: LineSegment StartX=11.6825 StartY=-38.256 StartZ=0 EndX=14.1566 EndY=-40.7301 EndZ=0
    g8: LineSegment StartX=13.8582 StartY=40.4317 StartZ=0 EndX=15.9795 EndY=38.3104 EndZ=0
    g9: GeomPoint X=15.2724 Y=39.0175 Z=0
    g10: LineSegment StartX=13.8582 StartY=-40.4317 StartZ=0 EndX=15.9795 EndY=-38.3104 EndZ=0
    g11: GeomPoint X=15.2724 Y=-39.0175 Z=0
    g12: LineSegment StartX=-41.9 StartY=1 StartZ=0 EndX=41.9 EndY=1 EndZ=0
    g13: LineSegment StartX=41.9 StartY=1 StartZ=0 EndX=41.9 EndY=-1 EndZ=0
    g14: LineSegment StartX=41.9 StartY=-1 StartZ=0 EndX=-41.9 EndY=-1 EndZ=0
    g15: LineSegment StartX=-41.9 StartY=-1 StartZ=0 EndX=-41.9 EndY=1 EndZ=0
    g16: GeomPoint X=-41.9 Y=0 Z=0
    g17: GeomPoint X=41.9 Y=0 Z=0
  constraints (51):
    c: Coincident(g0,g1)
    c: Coincident(g1,g2)
    c: Coincident(g2,g3)
    c: Coincident(g3,g0)
    c: Coincident(g4,g5)
    c: Coincident(g5,g6)
    c: Coincident(g6,g7)
    c: Coincident(g7,g4)
    c: Perpendicular(g-3,g0)
    c: Perpendicular(g-3,g2)
    c: Parallel(g1,g3)
    c: Parallel(g-3,g3)
    c: Parallel(g5,g7)
    c: Parallel(g7,g-4)
    c: Parallel(g4,g6)
    c: PointOnObject(g8,g3)
    c: PointOnObject(g8,g1)
    c: Perpendicular(g-3,g8)
    c: PointOnObject(g9,g8)
    c: PointOnObject(g9,g-3)
    c: Distance(g8,g9) = 1
    c: Distance(g8,g9) = 2
    c: PointOnObject(g2,g-5)
    c: Perpendicular(g-4,g6)
    c: PointOnObject(g6,g-5)
    c: PointOnObject(g10,g7)
    c: PointOnObject(g10,g5)
    c: Perpendicular(g-4,g10)
    c: PointOnObject(g11,g10)
    c: PointOnObject(g11,g-4)
    c: Distance(g10,g11) = 1
    c: Distance(g10,g11) = 2
    c: PointOnObject(g4,g-6)
    c: PointOnObject(g11,g-6)
    c: PointOnObject(g0,g-6)
    c: PointOnObject(g9,g-6)
    c: Coincident(g12,g13)
    c: Coincident(g13,g14)
    c: Coincident(g14,g15)
    c: Coincident(g15,g12)
    c: Horizontal(g12)
    c: Horizontal(g14)
    c: Vertical(g13)
    c: Symmetric(g12,g14,g-1)
    c: DistanceY(g13,g13) = 2
    c: PointOnObject(g16,g15)
    c: PointOnObject(g16,g-6)
    c: PointOnObject(g16,g-1)
    c: PointOnObject(g17,g13)
    c: PointOnObject(g17,g-1)
    c: PointOnObject(g17,g-6)
FEATURE [PartDesign::Pocket] Pocket003
  BaseFeature = -> Revolution002
  Direction = (0,0,-1)
  Length = 5
  Length2 = 5
  Placement = pos=(0,0,0) rot=(1,0,0;1.5708rad)
  Profile = -> Sketch306
  ReferenceAxis = -> Sketch306 [N_Axis]
  Reversed = true
  Type = 1
FEATURE [PartDesign::Body] Body022055  label="MirrorCover_625"
  Group = -> [ShapeBinder011,Sketch305,Revolution002,Sketch306,Pocket003]
  Origin = -> Origin110
  Placement = pos=(-3.125,0,0) rot=(0,0,1;0rad)
  Tip = -> Pocket003
  expr: .Placement.Base.x = -<<Common>>#<<Parameters>>.sec_offset_x
COMPONENT P8 — recipe-attached ("MirrorCoverCap_625", modeled in this document).
Construction recipe (the document's own serialized feature program — sketch geometry with constraints, then the solid features built on it; lengths are millimeters unless a unit is written):

FEATURE [Sketcher::SketchObject] Sketch307
  FullyConstrained = true
  MapMode = 5
  Placement = pos=(0,0,0) rot=(1,0,0;1.5708rad)
  Support = -> [XZ_Plane108]
  sketch-geometry (11):
    g0: LineSegment StartX=41.7 StartY=9.5 StartZ=0 EndX=42.9 EndY=9.5 EndZ=0
    g1: LineSegment StartX=42.9 StartY=9.5 StartZ=0 EndX=42.9 EndY=-0.6 EndZ=0
    g2: LineSegment StartX=8.5 StartY=-1.2 StartZ=0 EndX=8.5 EndY=0 EndZ=0
    g3: LineSegment StartX=41.2 StartY=8.5 StartZ=0 EndX=41.7 EndY=9.5 EndZ=0
    g4: LineSegment StartX=41.2 StartY=6.5 StartZ=0 EndX=41.2 EndY=8.5 EndZ=0
    g5: LineSegment StartX=41.7 StartY=0.6 StartZ=0 EndX=41.7 EndY=5 EndZ=0
    g6: LineSegment StartX=41.7 StartY=5 StartZ=0 EndX=41.2 EndY=6.5 EndZ=0
    g7: LineSegment StartX=8.5 StartY=0 StartZ=0 EndX=41.1 EndY=0 EndZ=0
    g8: LineSegment StartX=41.1 StartY=0 StartZ=0 EndX=41.7 EndY=0.6 EndZ=0
    g9: LineSegment StartX=42.9 StartY=-0.6 StartZ=0 EndX=42.3 EndY=-1.2 EndZ=0
    g10: LineSegment StartX=42.3 StartY=-1.2 StartZ=0 EndX=8.5 EndY=-1.2 EndZ=0
  constraints (33):
    c: PointOnObject(g7,g-1)
    c: Coincident(g5,g8)
    c: Coincident(g0,g3)
    c: Coincident(g1,g0)
    c: Vertical(g1)
    c: Coincident(g9,g1)
    c: Coincident(g2,g10)
    c: Coincident(g2,g7)
    c: Horizontal(g0)
    c: Vertical(g2)
    c: DistanceY(g2,g2) = 1.2
    c: DistanceX(g10) = 8.5
    c: Coincident(g4,g3)
    c: Coincident(g6,g4)
    c: Vertical(g4)
    c: Coincident(g5,g6)
    c: Vertical(g5)
    c: DistanceY(g4,g4) = 2
    c: DistanceX(g3,g0) = 0.5
    c: PointOnObject(g0,g5)
    c: DistanceY(g3,g0) = 1
    c: DistanceY(g6,g6) = 1.5
    c: DistanceX(g4) = 41.2
    c: Equal(g0,g2)
    c: Coincident(g7,g8)
    c: Horizontal(g7)
    c: Coincident(g9,g10)
    c: Horizontal(g10)
    c: DistanceY(g7,g5) = 5
    c: Equal(g9,g8)
    c: Parallel(g8,g9)
    c: Angle(g5,g8) = 2.35619
    c: DistanceY(g9,g1) = 0.6
FEATURE [PartDesign::Revolution] Revolution003
  Angle = 360
  Axis = (1e-16,1e-16,1)
  Base = (0,0,0)
  Placement = pos=(0,0,0) rot=(1,0,0;1.5708rad)
  Profile = -> Sketch307
  ReferenceAxis = -> Z_Axis108
  Reversed = true
FEATURE [Sketcher::SketchObject] Sketch308
  AttachmentOffset = pos=(0,0,5) rot=(0,0,1;0rad)
  ExternalGeometry = -> [Revolution003]
  FullyConstrained = true
  MapMode = 5
  Placement = pos=(0,0,5) rot=(0,0,1;0rad)
  Support = -> [XY_Plane107]
  sketch-geometry (17):
    g0: ArcOfCircle CenterX=1.1e-15 CenterY=1.1e-15 CenterZ=0 NormalX=0 NormalY=0 NormalZ=1 AngleXU=0 Radius=41.7 StartAngle=0.392699 EndAngle=1.1781
    g1: LineSegment StartX=38.5258 StartY=15.9579 StartZ=0 EndX=22.5679 EndY=0 EndZ=0
    g2: LineSegment StartX=22.5679 StartY=1.8e-15 StartZ=0 EndX=38.5258 EndY=-15.9579 EndZ=0
    g3: ArcOfCircle CenterX=1.1e-15 CenterY=1.1e-15 CenterZ=0 NormalX=0 NormalY=0 NormalZ=1 AngleXU=0 Radius=41.7 StartAngle=5.10509 EndAngle=5.89049
    g4: LineSegment StartX=15.9579 StartY=-38.5258 StartZ=0 EndX=1.8e-15 EndY=-22.5679 EndZ=0
    g5: LineSegment StartX=1.8e-15 StartY=-22.5679 StartZ=0 EndX=-15.9579 EndY=-38.5258 EndZ=0
    g6: ArcOfCircle CenterX=1.1e-15 CenterY=1.1e-15 CenterZ=0 NormalX=0 NormalY=0 NormalZ=1 AngleXU=0 Radius=41.7 StartAngle=3.53429 EndAngle=4.31969
    g7: LineSegment StartX=-38.5258 StartY=-15.9579 StartZ=0 EndX=-22.5679 EndY=0 EndZ=0
    g8: LineSegment StartX=-22.5679 StartY=0 StartZ=0 EndX=-38.5258 EndY=15.9579 EndZ=0
    g9: ArcOfCircle CenterX=1.1e-15 CenterY=1.1e-15 CenterZ=0 NormalX=0 NormalY=0 NormalZ=1 AngleXU=0 Radius=41.7 StartAngle=1.9635 EndAngle=2.74889
    g10: LineSegment StartX=-15.9579 StartY=38.5258 StartZ=0 EndX=0 EndY=22.5679 EndZ=0
    g11: LineSegment StartX=0 StartY=22.5679 StartZ=0 EndX=15.9579 EndY=38.5258 EndZ=0
    g12: LineSegment StartX=-15.9579 StartY=38.5258 StartZ=0 EndX=15.9579 EndY=38.5258 EndZ=0
    g13: LineSegment StartX=38.5258 StartY=15.9579 StartZ=0 EndX=38.5258 EndY=-15.9579 EndZ=0
    g14: LineSegment StartX=15.9579 StartY=-38.5258 StartZ=0 EndX=-15.9579 EndY=-38.5258 EndZ=0
    g15: LineSegment StartX=-38.5258 StartY=-15.9579 StartZ=0 EndX=-38.5258 EndY=15.9579 EndZ=0
    g16: LineSegment StartX=-38.5258 StartY=15.9579 StartZ=0 EndX=-15.9579 EndY=38.5258 EndZ=0
  constraints (46):
    c: Coincident(g0,g-3)
    c: Coincident(g1,g0)
    c: Perpendicular(g1,g2)
    c: Coincident(g2,g1)
    c: Equal(g2,g1)
    c: Coincident(g3,g0)
    c: Coincident(g3,g2)
    c: Coincident(g4,g3)
    c: Coincident(g5,g4)
    c: Coincident(g6,g0)
    c: Coincident(g6,g5)
    c: Coincident(g7,g6)
    c: Coincident(g8,g7)
    c: Coincident(g9,g0)
    c: Coincident(g9,g8)
    c: Coincident(g10,g9)
    c: Coincident(g11,g10)
    c: Coincident(g11,g0)
    c: Coincident(g12,g9)
    c: Coincident(g12,g0)
    c: Coincident(g13,g0)
    c: Coincident(g13,g2)
    c: Coincident(g14,g3)
    c: Coincident(g14,g5)
    c: Coincident(g15,g6)
    c: Coincident(g15,g8)
    c: Equal(g14,g15)
    c: Equal(g15,g13)
    c: Equal(g13,g12)
    c: Equal(g11,g10)
    c: Equal(g8,g7)
    c: Equal(g5,g4)
    c: Equal(g2,g5)
    c: Equal(g5,g8)
    c: Equal(g8,g11)
    c: PointOnObject(g2,g-3)
    c: PointOnObject(g5,g-3)
    c: PointOnObject(g8,g-3)
    c: PointOnObject(g0,g-3)
    c: PointOnObject(g10,g-2)
    c: PointOnObject(g7,g-1)
    c: PointOnObject(g1,g-1)
    c: PointOnObject(g4,g-2)
    c: Coincident(g16,g8)
    c: Coincident(g16,g9)
    c: Equal(g16,g12)
FEATURE [PartDesign::Pocket] Pocket004
  BaseFeature = -> Revolution003
  Direction = (0,0,-1)
  Length = 5
  Length2 = 5
  Placement = pos=(0,0,0) rot=(1,0,0;1.5708rad)
  Profile = -> Sketch308
  ReferenceAxis = -> Sketch308 [N_Axis]
  Reversed = true
  Type = 1
FEATURE [PartDesign::Body] Body022056  label="MirrorCoverCap_625"
  Group = -> [Sketch307,Revolution003,Sketch308,Pocket004]
  Origin = -> Origin111
  Tip = -> Pocket004
PROVENANCE & LICENSES
A FreeCAD (.FCStd) document from a public repository crawl; recipes are the document's own serialized feature recipes (and, for linked parts, companion documents' recipes).
License: as declared in the source repository (recorded in the dataset sidecar).
